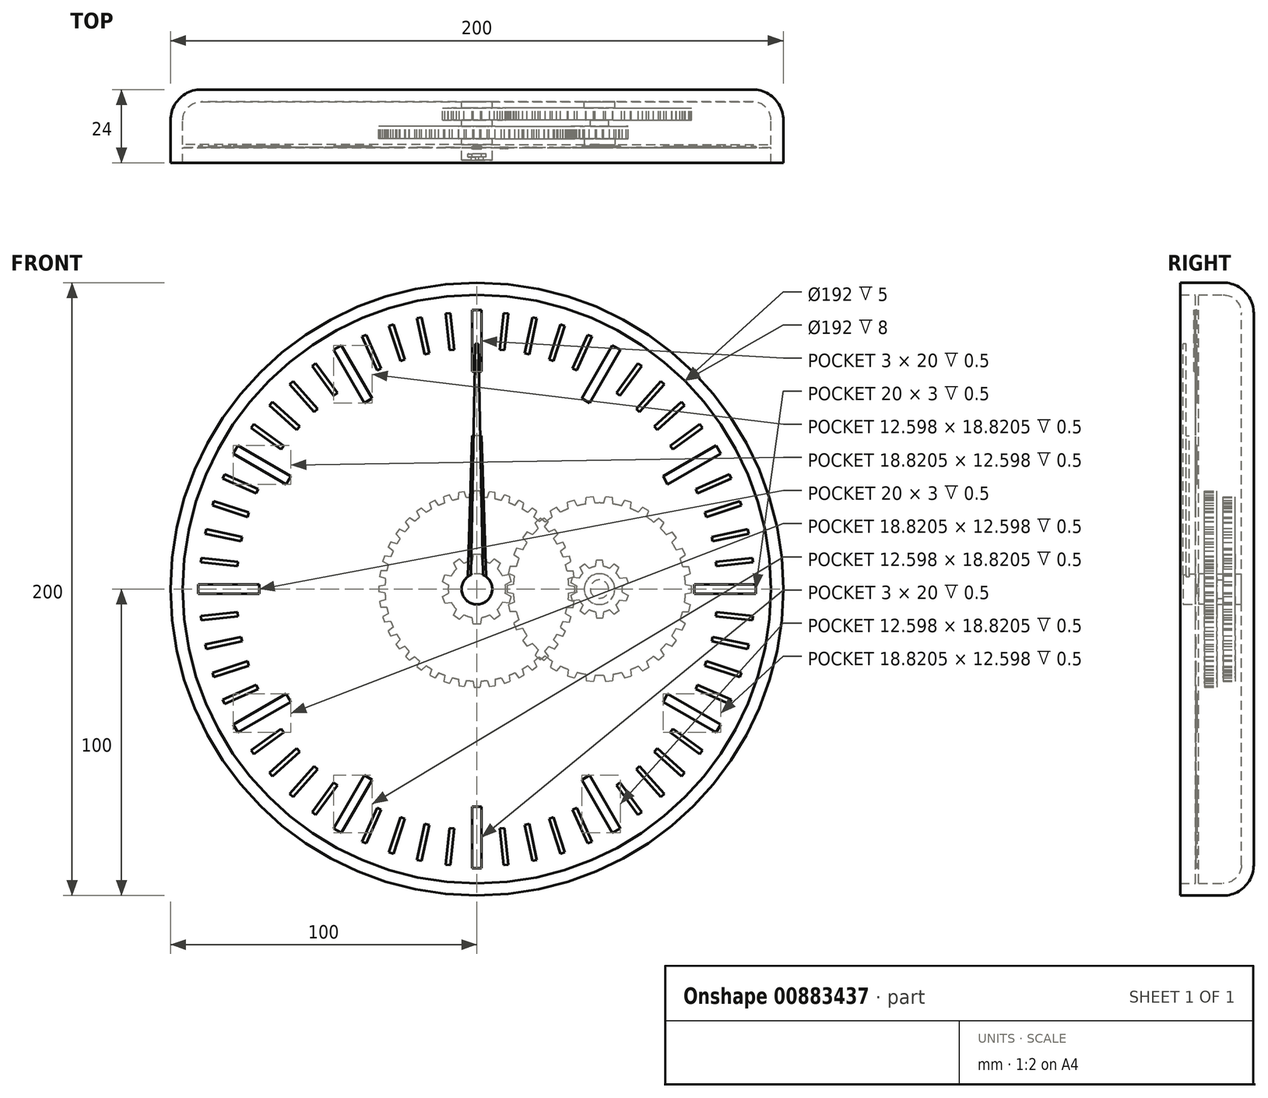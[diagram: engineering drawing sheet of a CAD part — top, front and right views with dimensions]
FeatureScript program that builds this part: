
annotation { "Feature Type Name" : "Feature", "Feature Type Description" : "" }
export const myFeature = defineFeature(function(context is Context, id is Id, definition is map)
    precondition{}
    {
        {
            var Q0;
            Q0=qCreatedBy(makeId("Front.planeOp"),FACE);
            var sketch = newSketch(context, id + "F0", { "sketchPlane" : qUnion([Q0])});
            skCircle(sketch, "E0", {"center": v(0, 0) * mm, "radius": 100 * mm});
            skSolve(sketch);
        }
        {
            var Q0;
            Q0 = qSketchRegion(id + "F0", true);
            extrude(context, id + "F1", {"entities" : qUnion([Q0]), "depth" : 24 * mm, "offsetDistance" : 25 * mm});
        }
        {
            var Q0;
            Q0=makeQuery(id+"F1.opExtrude","CAP_EDGE",EDGE,{"disambiguationData":[OSD([sQuery(id+"F0.wireOp",EDGE,"E0")])],"isStart":true});
            fillet(context, id + "F2", {"entities" : qUnion([Q0]), "radius" : 10 * mm, "tangentPropagation" : true, "allowEdgeOverflow" : false});
        }
        {
            var Q0;
            Q0=makeQuery(id+"F1.opExtrude","CAP_FACE",FACE,{"disambiguationData":[OSD([sQuery(id+"F0.wireOp",EDGE,"E0")])],"isStart":false});
            shell(context, id + "F3", {"entities" : qUnion([Q0]), "thickness" : 4 * mm});
        }
        {
            var Q0;
            {var subQ0=sQuery(id+"F0.wireOp",EDGE,"E0");Q0=makeQuery(id+"F3.opShell","OFFSET_FACE",FACE,{"disambiguationData":[OSD([subQ0]),TDD([makeQuery(id+"F1.opExtrude","CAP_FACE",FACE,{"disambiguationData":[OSD([subQ0])],"isStart":true})])]});}
            var sketch = newSketch(context, id + "F4", { "sketchPlane" : qUnion([Q0])});
            skCircle(sketch, "E1", {"center": v(0, 0) * mm, "radius": 3 * mm});
            skCircle(sketch, "E2", {"center": v(0, 0) * mm, "radius": 5 * mm});
            skCircle(sketch, "E3", {"center": v(40, 0) * mm, "radius": 3 * mm});
            skCircle(sketch, "E4", {"center": v(40, 0) * mm, "radius": 5 * mm});
            skSolve(sketch);
        }
        {
            var Q0;
            Q0 = qSketchRegion(id + "F4", true);
            extrude(context, id + "F5", {"entities" : qUnion([Q0]), "operationType" : NewBodyOperationType.ADD, "depth" : 2 * mm, "offsetDistance" : 25 * mm});
        }
        {
            var Q0;
            {var subQ0=sQuery(id+"F0.wireOp",EDGE,"E0");Q0=makeQuery(id+"F5.boolean.opBoolean","SPLIT",FACE,{"disambiguationData":[TD([makeQuery(id+"F5.opExtrude","SWEPT_FACE",FACE,{"disambiguationData":[OSD([sQuery(id+"F4.wireOp",EDGE,"E1")])]})])],"derivedFrom":makeQuery(id+"F3.opShell","OFFSET_FACE",FACE,{"disambiguationData":[OSD([subQ0]),TDD([makeQuery(id+"F1.opExtrude","CAP_FACE",FACE,{"disambiguationData":[OSD([subQ0])],"isStart":true})])]})});}
            extrude(context, id + "F6", {"entities" : qUnion([Q0]), "depth" : 19 * mm, "offsetDistance" : 25 * mm});
        }
        {
            var Q0;
            {var subQ0=sQuery(id+"F0.wireOp",EDGE,"E0");Q0=makeQuery(id+"F5.boolean.opBoolean","SPLIT",FACE,{"disambiguationData":[TD([makeQuery(id+"F5.opExtrude","SWEPT_FACE",FACE,{"disambiguationData":[OSD([sQuery(id+"F4.wireOp",EDGE,"E3")])]})])],"derivedFrom":makeQuery(id+"F3.opShell","OFFSET_FACE",FACE,{"disambiguationData":[OSD([subQ0]),TDD([makeQuery(id+"F1.opExtrude","CAP_FACE",FACE,{"disambiguationData":[OSD([subQ0])],"isStart":true})])]})});}
            extrude(context, id + "F7", {"entities" : qUnion([Q0]), "depth" : 8 * mm, "offsetDistance" : 25 * mm});
        }
        {
            var Q0;
            Q0=makeQuery(id+"F5.opExtrude","CAP_FACE",FACE,{"disambiguationData":[OSD([sQuery(id+"F4.wireOp",EDGE,"E1"),sQuery(id+"F4.wireOp",EDGE,"E2")])],"isStart":false});
            var sketch = newSketch(context, id + "F8", { "sketchPlane" : qUnion([Q0])});
            skCircle(sketch, "E5", {"center": v(0, 0) * mm, "radius": 9.38 * mm});
            skLineSegment(sketch, "E6", {"start": v(0, 11.38) * mm, "end": v(1.18, 11.38) * mm});
            skLineSegment(sketch, "E7", {"start": v(1.18, 11.38) * mm, "end": v(1.55, 9.25) * mm});
            skLineSegment(sketch, "E8.MirrorCS", {"start": v(0, 11.38) * mm, "end": v(-1.18, 11.38) * mm});
            skLineSegment(sketch, "E9.MirrorCS", {"start": v(-1.18, 11.38) * mm, "end": v(-1.55, 9.25) * mm});
            skLineSegment(sketch, "E10.1.0", {"start": v(-6.69, 9.2) * mm, "end": v(-5.73, 9.9) * mm});
            skLineSegment(sketch, "E10.1.1", {"start": v(-5.73, 9.9) * mm, "end": v(-4.18, 8.4) * mm});
            skLineSegment(sketch, "E10.1.2", {"start": v(-6.69, 9.2) * mm, "end": v(-7.64, 8.51) * mm});
            skLineSegment(sketch, "E10.1.3", {"start": v(-7.64, 8.51) * mm, "end": v(-6.7, 6.57) * mm});
            skLineSegment(sketch, "E10.2.0", {"start": v(-10.82, 3.52) * mm, "end": v(-10.45, 4.64) * mm});
            skLineSegment(sketch, "E10.2.1", {"start": v(-10.45, 4.64) * mm, "end": v(-8.31, 4.33) * mm});
            skLineSegment(sketch, "E10.2.2", {"start": v(-10.82, 3.52) * mm, "end": v(-11.18, 2.4) * mm});
            skLineSegment(sketch, "E10.2.3", {"start": v(-11.18, 2.4) * mm, "end": v(-9.27, 1.38) * mm});
            skLineSegment(sketch, "E11.1.3.0", {"start": v(-10.82, -3.52) * mm, "end": v(-11.18, -2.4) * mm});
            skLineSegment(sketch, "E11.3.3.0", {"start": v(-11.18, -2.4) * mm, "end": v(-9.27, -1.38) * mm});
            skLineSegment(sketch, "E11.6.3.0", {"start": v(-10.82, -3.52) * mm, "end": v(-10.45, -4.64) * mm});
            skLineSegment(sketch, "E11.9.3.0", {"start": v(-10.45, -4.64) * mm, "end": v(-8.31, -4.33) * mm});
            skLineSegment(sketch, "E11.1.4.0", {"start": v(-6.69, -9.2) * mm, "end": v(-7.64, -8.51) * mm});
            skLineSegment(sketch, "E11.3.4.0", {"start": v(-7.64, -8.51) * mm, "end": v(-6.7, -6.57) * mm});
            skLineSegment(sketch, "E11.6.4.0", {"start": v(-6.69, -9.2) * mm, "end": v(-5.73, -9.9) * mm});
            skLineSegment(sketch, "E11.9.4.0", {"start": v(-5.73, -9.9) * mm, "end": v(-4.18, -8.4) * mm});
            skLineSegment(sketch, "E11.1.5.0", {"start": v(0, -11.38) * mm, "end": v(-1.18, -11.38) * mm});
            skLineSegment(sketch, "E11.3.5.0", {"start": v(-1.18, -11.38) * mm, "end": v(-1.55, -9.25) * mm});
            skLineSegment(sketch, "E11.6.5.0", {"start": v(0, -11.38) * mm, "end": v(1.18, -11.38) * mm});
            skLineSegment(sketch, "E11.9.5.0", {"start": v(1.18, -11.38) * mm, "end": v(1.55, -9.25) * mm});
            skLineSegment(sketch, "E11.1.6.0", {"start": v(6.69, -9.2) * mm, "end": v(5.73, -9.9) * mm});
            skLineSegment(sketch, "E11.3.6.0", {"start": v(5.73, -9.9) * mm, "end": v(4.18, -8.4) * mm});
            skLineSegment(sketch, "E11.6.6.0", {"start": v(6.69, -9.2) * mm, "end": v(7.64, -8.51) * mm});
            skLineSegment(sketch, "E11.9.6.0", {"start": v(7.64, -8.51) * mm, "end": v(6.7, -6.57) * mm});
            skLineSegment(sketch, "E11.1.7.0", {"start": v(10.82, -3.52) * mm, "end": v(10.45, -4.64) * mm});
            skLineSegment(sketch, "E11.3.7.0", {"start": v(10.45, -4.64) * mm, "end": v(8.31, -4.33) * mm});
            skLineSegment(sketch, "E11.6.7.0", {"start": v(10.82, -3.52) * mm, "end": v(11.18, -2.4) * mm});
            skLineSegment(sketch, "E11.9.7.0", {"start": v(11.18, -2.4) * mm, "end": v(9.27, -1.38) * mm});
            skLineSegment(sketch, "E11.1.8.0", {"start": v(10.82, 3.52) * mm, "end": v(11.18, 2.4) * mm});
            skLineSegment(sketch, "E11.3.8.0", {"start": v(11.18, 2.4) * mm, "end": v(9.27, 1.38) * mm});
            skLineSegment(sketch, "E11.6.8.0", {"start": v(10.82, 3.52) * mm, "end": v(10.45, 4.64) * mm});
            skLineSegment(sketch, "E11.9.8.0", {"start": v(10.45, 4.64) * mm, "end": v(8.31, 4.33) * mm});
            skLineSegment(sketch, "E11.1.9.0", {"start": v(6.69, 9.2) * mm, "end": v(7.64, 8.51) * mm});
            skLineSegment(sketch, "E11.3.9.0", {"start": v(7.64, 8.51) * mm, "end": v(6.7, 6.57) * mm});
            skLineSegment(sketch, "E11.6.9.0", {"start": v(6.69, 9.2) * mm, "end": v(5.73, 9.9) * mm});
            skLineSegment(sketch, "E11.9.9.0", {"start": v(5.73, 9.9) * mm, "end": v(4.18, 8.4) * mm});
            skSolve(sketch);
        }
        {
            var Q0;
            Q0 = qSketchRegion(id + "F8", true);
            extrude(context, id + "F9", {"entities" : qUnion([Q0]), "operationType" : NewBodyOperationType.ADD, "depth" : 4 * mm, "offsetDistance" : 25 * mm});
        }
        {
            var Q0;
            Q0=makeQuery(id+"F5.opExtrude","CAP_FACE",FACE,{"disambiguationData":[OSD([sQuery(id+"F4.wireOp",EDGE,"E3"),sQuery(id+"F4.wireOp",EDGE,"E4")])],"isStart":false});
            var sketch = newSketch(context, id + "F10", { "sketchPlane" : qUnion([Q0])});
            skCircle(sketch, "E12", {"center": v(40, 0) * mm, "radius": 28.12 * mm});
            skLineSegment(sketch, "E13", {"start": v(11.92, 1.54) * mm, "end": v(9.88, 1.18) * mm});
            skLineSegment(sketch, "E14", {"start": v(9.88, 1.18) * mm, "end": v(9.88, 0) * mm});
            skLineSegment(sketch, "E15.MirrorCS", {"start": v(9.88, -1.18) * mm, "end": v(9.88, 0) * mm});
            skLineSegment(sketch, "E16.MirrorCS", {"start": v(11.92, -1.54) * mm, "end": v(9.88, -1.18) * mm});
            skLineSegment(sketch, "E17.1.0", {"start": v(12.21, -4.33) * mm, "end": v(10.29, -5.11) * mm});
            skLineSegment(sketch, "E17.1.1", {"start": v(10.29, -5.11) * mm, "end": v(10.53, -6.26) * mm});
            skLineSegment(sketch, "E17.1.2", {"start": v(10.78, -7.42) * mm, "end": v(10.53, -6.26) * mm});
            skLineSegment(sketch, "E17.1.3", {"start": v(12.85, -7.34) * mm, "end": v(10.78, -7.42) * mm});
            skLineSegment(sketch, "E17.2.0", {"start": v(13.72, -10.02) * mm, "end": v(12, -11.18) * mm});
            skLineSegment(sketch, "E17.2.1", {"start": v(12, -11.18) * mm, "end": v(12.48, -12.25) * mm});
            skLineSegment(sketch, "E17.2.2", {"start": v(12.96, -13.33) * mm, "end": v(12.48, -12.25) * mm});
            skLineSegment(sketch, "E17.2.3", {"start": v(14.97, -12.83) * mm, "end": v(12.96, -13.33) * mm});
            skLineSegment(sketch, "E18.2.3.0", {"start": v(16.38, -15.26) * mm, "end": v(14.94, -16.75) * mm});
            skLineSegment(sketch, "E18.3.3.0", {"start": v(14.94, -16.75) * mm, "end": v(15.63, -17.7) * mm});
            skLineSegment(sketch, "E18.6.3.0", {"start": v(16.32, -18.66) * mm, "end": v(15.63, -17.7) * mm});
            skLineSegment(sketch, "E18.9.3.0", {"start": v(18.18, -17.75) * mm, "end": v(16.32, -18.66) * mm});
            skLineSegment(sketch, "E18.2.4.0", {"start": v(20.07, -19.84) * mm, "end": v(18.97, -21.6) * mm});
            skLineSegment(sketch, "E18.3.4.0", {"start": v(18.97, -21.6) * mm, "end": v(19.84, -22.39) * mm});
            skLineSegment(sketch, "E18.6.4.0", {"start": v(20.72, -23.18) * mm, "end": v(19.84, -22.39) * mm});
            skLineSegment(sketch, "E18.9.4.0", {"start": v(22.35, -21.9) * mm, "end": v(20.72, -23.18) * mm});
            skLineSegment(sketch, "E18.2.5.0", {"start": v(24.63, -23.55) * mm, "end": v(23.92, -25.5) * mm});
            skLineSegment(sketch, "E18.3.5.0", {"start": v(23.92, -25.5) * mm, "end": v(24.94, -26.09) * mm});
            skLineSegment(sketch, "E18.6.5.0", {"start": v(25.96, -26.68) * mm, "end": v(24.94, -26.09) * mm});
            skLineSegment(sketch, "E18.9.5.0", {"start": v(27.3, -25.09) * mm, "end": v(25.96, -26.68) * mm});
            skLineSegment(sketch, "E18.2.6.0", {"start": v(29.86, -26.23) * mm, "end": v(29.57, -28.29) * mm});
            skLineSegment(sketch, "E18.3.6.0", {"start": v(29.57, -28.29) * mm, "end": v(30.7, -28.65) * mm});
            skLineSegment(sketch, "E18.6.6.0", {"start": v(31.81, -29.01) * mm, "end": v(30.7, -28.65) * mm});
            skLineSegment(sketch, "E18.9.6.0", {"start": v(32.78, -27.18) * mm, "end": v(31.81, -29.01) * mm});
            skLineSegment(sketch, "E18.2.7.0", {"start": v(35.53, -27.77) * mm, "end": v(35.68, -29.84) * mm});
            skLineSegment(sketch, "E18.3.7.0", {"start": v(35.68, -29.84) * mm, "end": v(36.85, -29.96) * mm});
            skLineSegment(sketch, "E18.6.7.0", {"start": v(38.02, -30.08) * mm, "end": v(36.85, -29.96) * mm});
            skLineSegment(sketch, "E18.9.7.0", {"start": v(38.6, -28.09) * mm, "end": v(38.02, -30.08) * mm});
            skLineSegment(sketch, "E18.2.8.0", {"start": v(41.4, -28.09) * mm, "end": v(41.98, -30.08) * mm});
            skLineSegment(sketch, "E18.3.8.0", {"start": v(41.98, -30.08) * mm, "end": v(43.15, -29.96) * mm});
            skLineSegment(sketch, "E18.6.8.0", {"start": v(44.32, -29.84) * mm, "end": v(43.15, -29.96) * mm});
            skLineSegment(sketch, "E18.9.8.0", {"start": v(44.47, -27.77) * mm, "end": v(44.32, -29.84) * mm});
            skLineSegment(sketch, "E18.2.9.0", {"start": v(47.22, -27.18) * mm, "end": v(48.19, -29.01) * mm});
            skLineSegment(sketch, "E18.3.9.0", {"start": v(48.19, -29.01) * mm, "end": v(49.3, -28.65) * mm});
            skLineSegment(sketch, "E18.6.9.0", {"start": v(50.43, -28.29) * mm, "end": v(49.3, -28.65) * mm});
            skLineSegment(sketch, "E18.9.9.0", {"start": v(50.14, -26.23) * mm, "end": v(50.43, -28.29) * mm});
            skLineSegment(sketch, "E18.2.10.0", {"start": v(52.7, -25.09) * mm, "end": v(54.04, -26.68) * mm});
            skLineSegment(sketch, "E18.3.10.0", {"start": v(54.04, -26.68) * mm, "end": v(55.06, -26.09) * mm});
            skLineSegment(sketch, "E18.6.10.0", {"start": v(56.08, -25.5) * mm, "end": v(55.06, -26.09) * mm});
            skLineSegment(sketch, "E18.9.10.0", {"start": v(55.37, -23.55) * mm, "end": v(56.08, -25.5) * mm});
            skLineSegment(sketch, "E18.2.11.0", {"start": v(57.65, -21.9) * mm, "end": v(59.28, -23.18) * mm});
            skLineSegment(sketch, "E18.3.11.0", {"start": v(59.28, -23.18) * mm, "end": v(60.16, -22.39) * mm});
            skLineSegment(sketch, "E18.6.11.0", {"start": v(61.03, -21.6) * mm, "end": v(60.16, -22.39) * mm});
            skLineSegment(sketch, "E18.9.11.0", {"start": v(59.93, -19.84) * mm, "end": v(61.03, -21.6) * mm});
            skLineSegment(sketch, "E18.2.12.0", {"start": v(61.82, -17.75) * mm, "end": v(63.68, -18.66) * mm});
            skLineSegment(sketch, "E18.3.12.0", {"start": v(63.68, -18.66) * mm, "end": v(64.37, -17.7) * mm});
            skLineSegment(sketch, "E18.6.12.0", {"start": v(65.06, -16.75) * mm, "end": v(64.37, -17.7) * mm});
            skLineSegment(sketch, "E18.9.12.0", {"start": v(63.62, -15.26) * mm, "end": v(65.06, -16.75) * mm});
            skLineSegment(sketch, "E18.2.13.0", {"start": v(65.03, -12.83) * mm, "end": v(67.04, -13.33) * mm});
            skLineSegment(sketch, "E18.3.13.0", {"start": v(67.04, -13.33) * mm, "end": v(67.52, -12.25) * mm});
            skLineSegment(sketch, "E18.6.13.0", {"start": v(68, -11.18) * mm, "end": v(67.52, -12.25) * mm});
            skLineSegment(sketch, "E18.9.13.0", {"start": v(66.28, -10.02) * mm, "end": v(68, -11.18) * mm});
            skLineSegment(sketch, "E18.2.14.0", {"start": v(67.15, -7.34) * mm, "end": v(69.22, -7.42) * mm});
            skLineSegment(sketch, "E18.3.14.0", {"start": v(69.22, -7.42) * mm, "end": v(69.47, -6.26) * mm});
            skLineSegment(sketch, "E18.6.14.0", {"start": v(69.71, -5.11) * mm, "end": v(69.47, -6.26) * mm});
            skLineSegment(sketch, "E18.9.14.0", {"start": v(67.79, -4.33) * mm, "end": v(69.71, -5.11) * mm});
            skLineSegment(sketch, "E18.2.15.0", {"start": v(68.08, -1.54) * mm, "end": v(70.12, -1.18) * mm});
            skLineSegment(sketch, "E18.3.15.0", {"start": v(70.12, -1.18) * mm, "end": v(70.12, 0) * mm});
            skLineSegment(sketch, "E18.6.15.0", {"start": v(70.12, 1.18) * mm, "end": v(70.12, 0) * mm});
            skLineSegment(sketch, "E18.9.15.0", {"start": v(68.08, 1.54) * mm, "end": v(70.12, 1.18) * mm});
            skLineSegment(sketch, "E18.2.16.0", {"start": v(67.79, 4.33) * mm, "end": v(69.71, 5.11) * mm});
            skLineSegment(sketch, "E18.3.16.0", {"start": v(69.71, 5.11) * mm, "end": v(69.47, 6.26) * mm});
            skLineSegment(sketch, "E18.6.16.0", {"start": v(69.22, 7.42) * mm, "end": v(69.47, 6.26) * mm});
            skLineSegment(sketch, "E18.9.16.0", {"start": v(67.15, 7.34) * mm, "end": v(69.22, 7.42) * mm});
            skLineSegment(sketch, "E18.2.17.0", {"start": v(66.28, 10.02) * mm, "end": v(68, 11.18) * mm});
            skLineSegment(sketch, "E18.3.17.0", {"start": v(68, 11.18) * mm, "end": v(67.52, 12.25) * mm});
            skLineSegment(sketch, "E18.6.17.0", {"start": v(67.04, 13.33) * mm, "end": v(67.52, 12.25) * mm});
            skLineSegment(sketch, "E18.9.17.0", {"start": v(65.03, 12.83) * mm, "end": v(67.04, 13.33) * mm});
            skLineSegment(sketch, "E18.2.18.0", {"start": v(63.62, 15.26) * mm, "end": v(65.06, 16.75) * mm});
            skLineSegment(sketch, "E18.3.18.0", {"start": v(65.06, 16.75) * mm, "end": v(64.37, 17.7) * mm});
            skLineSegment(sketch, "E18.6.18.0", {"start": v(63.68, 18.66) * mm, "end": v(64.37, 17.7) * mm});
            skLineSegment(sketch, "E18.9.18.0", {"start": v(61.82, 17.75) * mm, "end": v(63.68, 18.66) * mm});
            skLineSegment(sketch, "E18.2.19.0", {"start": v(59.93, 19.84) * mm, "end": v(61.03, 21.6) * mm});
            skLineSegment(sketch, "E18.3.19.0", {"start": v(61.03, 21.6) * mm, "end": v(60.16, 22.39) * mm});
            skLineSegment(sketch, "E18.6.19.0", {"start": v(59.28, 23.18) * mm, "end": v(60.16, 22.39) * mm});
            skLineSegment(sketch, "E18.9.19.0", {"start": v(57.65, 21.9) * mm, "end": v(59.28, 23.18) * mm});
            skLineSegment(sketch, "E18.2.20.0", {"start": v(55.37, 23.55) * mm, "end": v(56.08, 25.5) * mm});
            skLineSegment(sketch, "E18.3.20.0", {"start": v(56.08, 25.5) * mm, "end": v(55.06, 26.09) * mm});
            skLineSegment(sketch, "E18.6.20.0", {"start": v(54.04, 26.68) * mm, "end": v(55.06, 26.09) * mm});
            skLineSegment(sketch, "E18.9.20.0", {"start": v(52.7, 25.09) * mm, "end": v(54.04, 26.68) * mm});
            skLineSegment(sketch, "E18.2.21.0", {"start": v(50.14, 26.23) * mm, "end": v(50.43, 28.29) * mm});
            skLineSegment(sketch, "E18.3.21.0", {"start": v(50.43, 28.29) * mm, "end": v(49.3, 28.65) * mm});
            skLineSegment(sketch, "E18.6.21.0", {"start": v(48.19, 29.01) * mm, "end": v(49.3, 28.65) * mm});
            skLineSegment(sketch, "E18.9.21.0", {"start": v(47.22, 27.18) * mm, "end": v(48.19, 29.01) * mm});
            skLineSegment(sketch, "E18.2.22.0", {"start": v(44.47, 27.77) * mm, "end": v(44.32, 29.84) * mm});
            skLineSegment(sketch, "E18.3.22.0", {"start": v(44.32, 29.84) * mm, "end": v(43.15, 29.96) * mm});
            skLineSegment(sketch, "E18.6.22.0", {"start": v(41.98, 30.08) * mm, "end": v(43.15, 29.96) * mm});
            skLineSegment(sketch, "E18.9.22.0", {"start": v(41.4, 28.09) * mm, "end": v(41.98, 30.08) * mm});
            skLineSegment(sketch, "E18.2.23.0", {"start": v(38.6, 28.09) * mm, "end": v(38.02, 30.08) * mm});
            skLineSegment(sketch, "E18.3.23.0", {"start": v(38.02, 30.08) * mm, "end": v(36.85, 29.96) * mm});
            skLineSegment(sketch, "E18.6.23.0", {"start": v(35.68, 29.84) * mm, "end": v(36.85, 29.96) * mm});
            skLineSegment(sketch, "E18.9.23.0", {"start": v(35.53, 27.77) * mm, "end": v(35.68, 29.84) * mm});
            skLineSegment(sketch, "E18.2.24.0", {"start": v(32.78, 27.18) * mm, "end": v(31.81, 29.01) * mm});
            skLineSegment(sketch, "E18.3.24.0", {"start": v(31.81, 29.01) * mm, "end": v(30.7, 28.65) * mm});
            skLineSegment(sketch, "E18.6.24.0", {"start": v(29.57, 28.29) * mm, "end": v(30.7, 28.65) * mm});
            skLineSegment(sketch, "E18.9.24.0", {"start": v(29.86, 26.23) * mm, "end": v(29.57, 28.29) * mm});
            skLineSegment(sketch, "E18.2.25.0", {"start": v(27.3, 25.09) * mm, "end": v(25.96, 26.68) * mm});
            skLineSegment(sketch, "E18.3.25.0", {"start": v(25.96, 26.68) * mm, "end": v(24.94, 26.09) * mm});
            skLineSegment(sketch, "E18.6.25.0", {"start": v(23.92, 25.5) * mm, "end": v(24.94, 26.09) * mm});
            skLineSegment(sketch, "E18.9.25.0", {"start": v(24.63, 23.55) * mm, "end": v(23.92, 25.5) * mm});
            skLineSegment(sketch, "E18.2.26.0", {"start": v(22.35, 21.9) * mm, "end": v(20.72, 23.18) * mm});
            skLineSegment(sketch, "E18.3.26.0", {"start": v(20.72, 23.18) * mm, "end": v(19.84, 22.39) * mm});
            skLineSegment(sketch, "E18.6.26.0", {"start": v(18.97, 21.6) * mm, "end": v(19.84, 22.39) * mm});
            skLineSegment(sketch, "E18.9.26.0", {"start": v(20.07, 19.84) * mm, "end": v(18.97, 21.6) * mm});
            skLineSegment(sketch, "E18.2.27.0", {"start": v(18.18, 17.75) * mm, "end": v(16.32, 18.66) * mm});
            skLineSegment(sketch, "E18.3.27.0", {"start": v(16.32, 18.66) * mm, "end": v(15.63, 17.7) * mm});
            skLineSegment(sketch, "E18.6.27.0", {"start": v(14.94, 16.75) * mm, "end": v(15.63, 17.7) * mm});
            skLineSegment(sketch, "E18.9.27.0", {"start": v(16.38, 15.26) * mm, "end": v(14.94, 16.75) * mm});
            skLineSegment(sketch, "E18.2.28.0", {"start": v(14.97, 12.83) * mm, "end": v(12.96, 13.33) * mm});
            skLineSegment(sketch, "E18.3.28.0", {"start": v(12.96, 13.33) * mm, "end": v(12.48, 12.25) * mm});
            skLineSegment(sketch, "E18.6.28.0", {"start": v(12, 11.18) * mm, "end": v(12.48, 12.25) * mm});
            skLineSegment(sketch, "E18.9.28.0", {"start": v(13.72, 10.02) * mm, "end": v(12, 11.18) * mm});
            skLineSegment(sketch, "E18.2.29.0", {"start": v(12.85, 7.34) * mm, "end": v(10.78, 7.42) * mm});
            skLineSegment(sketch, "E18.3.29.0", {"start": v(10.78, 7.42) * mm, "end": v(10.53, 6.26) * mm});
            skLineSegment(sketch, "E18.6.29.0", {"start": v(10.29, 5.11) * mm, "end": v(10.53, 6.26) * mm});
            skLineSegment(sketch, "E18.9.29.0", {"start": v(12.21, 4.33) * mm, "end": v(10.29, 5.11) * mm});
            skSolve(sketch);
        }
        {
            var Q0;
            Q0 = qSketchRegion(id + "F10", true);
            extrude(context, id + "F11", {"entities" : qUnion([Q0]), "operationType" : NewBodyOperationType.ADD, "depth" : 4 * mm, "offsetDistance" : 25 * mm});
        }
        {
            var Q0;
            Q0=makeQuery(id+"F9.opExtrude","CAP_FACE",FACE,{"disambiguationData":[OSD([sQuery(id+"F8.wireOp",EDGE,"E5"),sQuery(id+"F8.wireOp",EDGE,"E6"),sQuery(id+"F8.wireOp",EDGE,"E7"),sQuery(id+"F8.wireOp",EDGE,"E8.MirrorCS"),sQuery(id+"F8.wireOp",EDGE,"E9.MirrorCS"),sQuery(id+"F8.wireOp",EDGE,"E10.1.0"),sQuery(id+"F8.wireOp",EDGE,"E10.1.1"),sQuery(id+"F8.wireOp",EDGE,"E10.1.2"),sQuery(id+"F8.wireOp",EDGE,"E10.1.3"),sQuery(id+"F8.wireOp",EDGE,"E10.2.0"),sQuery(id+"F8.wireOp",EDGE,"E10.2.1"),sQuery(id+"F8.wireOp",EDGE,"E10.2.2"),sQuery(id+"F8.wireOp",EDGE,"E10.2.3"),sQuery(id+"F8.wireOp",EDGE,"E11.1.3.0"),sQuery(id+"F8.wireOp",EDGE,"E11.3.3.0"),sQuery(id+"F8.wireOp",EDGE,"E11.6.3.0"),sQuery(id+"F8.wireOp",EDGE,"E11.9.3.0"),sQuery(id+"F8.wireOp",EDGE,"E11.1.4.0"),sQuery(id+"F8.wireOp",EDGE,"E11.3.4.0"),sQuery(id+"F8.wireOp",EDGE,"E11.6.4.0"),sQuery(id+"F8.wireOp",EDGE,"E11.9.4.0"),sQuery(id+"F8.wireOp",EDGE,"E11.1.5.0"),sQuery(id+"F8.wireOp",EDGE,"E11.3.5.0"),sQuery(id+"F8.wireOp",EDGE,"E11.6.5.0"),sQuery(id+"F8.wireOp",EDGE,"E11.9.5.0"),sQuery(id+"F8.wireOp",EDGE,"E11.1.6.0"),sQuery(id+"F8.wireOp",EDGE,"E11.3.6.0"),sQuery(id+"F8.wireOp",EDGE,"E11.6.6.0"),sQuery(id+"F8.wireOp",EDGE,"E11.9.6.0"),sQuery(id+"F8.wireOp",EDGE,"E11.1.7.0"),sQuery(id+"F8.wireOp",EDGE,"E11.3.7.0"),sQuery(id+"F8.wireOp",EDGE,"E11.6.7.0"),sQuery(id+"F8.wireOp",EDGE,"E11.9.7.0"),sQuery(id+"F8.wireOp",EDGE,"E11.1.8.0"),sQuery(id+"F8.wireOp",EDGE,"E11.3.8.0"),sQuery(id+"F8.wireOp",EDGE,"E11.6.8.0"),sQuery(id+"F8.wireOp",EDGE,"E11.9.8.0"),sQuery(id+"F8.wireOp",EDGE,"E11.1.9.0"),sQuery(id+"F8.wireOp",EDGE,"E11.3.9.0"),sQuery(id+"F8.wireOp",EDGE,"E11.6.9.0"),sQuery(id+"F8.wireOp",EDGE,"E11.9.9.0")])],"isStart":false});
            var sketch = newSketch(context, id + "F12", { "sketchPlane" : qUnion([Q0])});
            skCircle(sketch, "E19.0", {"center": v(0, 0) * mm, "radius": 5 * mm});
            skCircle(sketch, "E20.0", {"center": v(0, 0) * mm, "radius": 3 * mm});
            skSolve(sketch);
        }
        {
            var Q0;
            Q0 = qSketchRegion(id + "F12", true);
            extrude(context, id + "F13", {"entities" : qUnion([Q0]), "depth" : 2 * mm, "offsetDistance" : 25 * mm});
        }
        {
            var Q0;
            Q0=makeQuery(id+"F13.opExtrude","CAP_FACE",FACE,{"disambiguationData":[OSD([sQuery(id+"F12.wireOp",EDGE,"E19.0"),sQuery(id+"F12.wireOp",EDGE,"E20.0")])],"isStart":false});
            var sketch = newSketch(context, id + "F14", { "sketchPlane" : qUnion([Q0])});
            skCircle(sketch, "E21.0", {"center": v(0, 0) * mm, "radius": 3 * mm});
            skCircle(sketch, "E22", {"center": v(0, 0) * mm, "radius": 30 * mm});
            skLineSegment(sketch, "E23", {"start": v(1.3, 29.97) * mm, "end": v(0.94, 32) * mm});
            skLineSegment(sketch, "E24", {"start": v(0.94, 32) * mm, "end": v(0, 32) * mm});
            skLineSegment(sketch, "E25.MirrorCS", {"start": v(-1.3, 29.97) * mm, "end": v(-0.94, 32) * mm});
            skLineSegment(sketch, "E26.MirrorCS", {"start": v(-0.94, 32) * mm, "end": v(0, 32) * mm});
            skLineSegment(sketch, "E27.1.0", {"start": v(-5.94, 31.46) * mm, "end": v(-5, 31.6) * mm});
            skLineSegment(sketch, "E27.1.1", {"start": v(-4.08, 31.75) * mm, "end": v(-5, 31.6) * mm});
            skLineSegment(sketch, "E27.1.2", {"start": v(-3.4, 29.8) * mm, "end": v(-4.08, 31.75) * mm});
            skLineSegment(sketch, "E27.1.3", {"start": v(-5.97, 29.4) * mm, "end": v(-5.94, 31.46) * mm});
            skLineSegment(sketch, "E27.2.0", {"start": v(-10.78, 30.14) * mm, "end": v(-9.89, 30.43) * mm});
            skLineSegment(sketch, "E27.2.1", {"start": v(-9, 30.73) * mm, "end": v(-9.89, 30.43) * mm});
            skLineSegment(sketch, "E27.2.2", {"start": v(-8.03, 28.9) * mm, "end": v(-9, 30.73) * mm});
            skLineSegment(sketch, "E27.2.3", {"start": v(-10.5, 28.1) * mm, "end": v(-10.78, 30.14) * mm});
            skLineSegment(sketch, "E28.1.3.0", {"start": v(-15.37, 28.08) * mm, "end": v(-14.53, 28.51) * mm});
            skLineSegment(sketch, "E28.3.3.0", {"start": v(-13.69, 28.94) * mm, "end": v(-14.53, 28.51) * mm});
            skLineSegment(sketch, "E28.6.3.0", {"start": v(-12.45, 27.3) * mm, "end": v(-13.69, 28.94) * mm});
            skLineSegment(sketch, "E28.9.3.0", {"start": v(-14.77, 26.11) * mm, "end": v(-15.37, 28.08) * mm});
            skLineSegment(sketch, "E28.1.4.0", {"start": v(-19.57, 25.33) * mm, "end": v(-18.8, 25.89) * mm});
            skLineSegment(sketch, "E28.3.4.0", {"start": v(-18.05, 26.44) * mm, "end": v(-18.8, 25.89) * mm});
            skLineSegment(sketch, "E28.6.4.0", {"start": v(-16.57, 25.01) * mm, "end": v(-18.05, 26.44) * mm});
            skLineSegment(sketch, "E28.9.4.0", {"start": v(-18.67, 23.48) * mm, "end": v(-19.57, 25.33) * mm});
            skLineSegment(sketch, "E28.1.5.0", {"start": v(-23.3, 21.96) * mm, "end": v(-22.63, 22.63) * mm});
            skLineSegment(sketch, "E28.3.5.0", {"start": v(-21.96, 23.3) * mm, "end": v(-22.63, 22.63) * mm});
            skLineSegment(sketch, "E28.6.5.0", {"start": v(-20.27, 22.11) * mm, "end": v(-21.96, 23.3) * mm});
            skLineSegment(sketch, "E28.9.5.0", {"start": v(-22.11, 20.27) * mm, "end": v(-23.3, 21.96) * mm});
            skLineSegment(sketch, "E28.1.6.0", {"start": v(-26.44, 18.05) * mm, "end": v(-25.89, 18.8) * mm});
            skLineSegment(sketch, "E28.3.6.0", {"start": v(-25.33, 19.57) * mm, "end": v(-25.89, 18.8) * mm});
            skLineSegment(sketch, "E28.6.6.0", {"start": v(-23.48, 18.67) * mm, "end": v(-25.33, 19.57) * mm});
            skLineSegment(sketch, "E28.9.6.0", {"start": v(-25.01, 16.57) * mm, "end": v(-26.44, 18.05) * mm});
            skLineSegment(sketch, "E28.1.7.0", {"start": v(-28.94, 13.69) * mm, "end": v(-28.51, 14.53) * mm});
            skLineSegment(sketch, "E28.3.7.0", {"start": v(-28.08, 15.37) * mm, "end": v(-28.51, 14.53) * mm});
            skLineSegment(sketch, "E28.6.7.0", {"start": v(-26.11, 14.77) * mm, "end": v(-28.08, 15.37) * mm});
            skLineSegment(sketch, "E28.9.7.0", {"start": v(-27.3, 12.45) * mm, "end": v(-28.94, 13.69) * mm});
            skLineSegment(sketch, "E28.1.8.0", {"start": v(-30.73, 9) * mm, "end": v(-30.43, 9.89) * mm});
            skLineSegment(sketch, "E28.3.8.0", {"start": v(-30.14, 10.78) * mm, "end": v(-30.43, 9.89) * mm});
            skLineSegment(sketch, "E28.6.8.0", {"start": v(-28.1, 10.5) * mm, "end": v(-30.14, 10.78) * mm});
            skLineSegment(sketch, "E28.9.8.0", {"start": v(-28.9, 8.03) * mm, "end": v(-30.73, 9) * mm});
            skLineSegment(sketch, "E28.1.9.0", {"start": v(-31.75, 4.08) * mm, "end": v(-31.6, 5) * mm});
            skLineSegment(sketch, "E28.3.9.0", {"start": v(-31.46, 5.94) * mm, "end": v(-31.6, 5) * mm});
            skLineSegment(sketch, "E28.6.9.0", {"start": v(-29.4, 5.97) * mm, "end": v(-31.46, 5.94) * mm});
            skLineSegment(sketch, "E28.9.9.0", {"start": v(-29.8, 3.4) * mm, "end": v(-31.75, 4.08) * mm});
            skLineSegment(sketch, "E28.1.10.0", {"start": v(-32, -0.94) * mm, "end": v(-32, 0) * mm});
            skLineSegment(sketch, "E28.3.10.0", {"start": v(-32, 0.94) * mm, "end": v(-32, 0) * mm});
            skLineSegment(sketch, "E28.6.10.0", {"start": v(-29.97, 1.3) * mm, "end": v(-32, 0.94) * mm});
            skLineSegment(sketch, "E28.9.10.0", {"start": v(-29.97, -1.3) * mm, "end": v(-32, -0.94) * mm});
            skLineSegment(sketch, "E28.1.11.0", {"start": v(-31.46, -5.94) * mm, "end": v(-31.6, -5) * mm});
            skLineSegment(sketch, "E28.3.11.0", {"start": v(-31.75, -4.08) * mm, "end": v(-31.6, -5) * mm});
            skLineSegment(sketch, "E28.6.11.0", {"start": v(-29.8, -3.4) * mm, "end": v(-31.75, -4.08) * mm});
            skLineSegment(sketch, "E28.9.11.0", {"start": v(-29.4, -5.97) * mm, "end": v(-31.46, -5.94) * mm});
            skLineSegment(sketch, "E28.1.12.0", {"start": v(-30.14, -10.78) * mm, "end": v(-30.43, -9.89) * mm});
            skLineSegment(sketch, "E28.3.12.0", {"start": v(-30.73, -9) * mm, "end": v(-30.43, -9.89) * mm});
            skLineSegment(sketch, "E28.6.12.0", {"start": v(-28.9, -8.03) * mm, "end": v(-30.73, -9) * mm});
            skLineSegment(sketch, "E28.9.12.0", {"start": v(-28.1, -10.5) * mm, "end": v(-30.14, -10.78) * mm});
            skLineSegment(sketch, "E28.1.13.0", {"start": v(-28.08, -15.37) * mm, "end": v(-28.51, -14.53) * mm});
            skLineSegment(sketch, "E28.3.13.0", {"start": v(-28.94, -13.69) * mm, "end": v(-28.51, -14.53) * mm});
            skLineSegment(sketch, "E28.6.13.0", {"start": v(-27.3, -12.45) * mm, "end": v(-28.94, -13.69) * mm});
            skLineSegment(sketch, "E28.9.13.0", {"start": v(-26.11, -14.77) * mm, "end": v(-28.08, -15.37) * mm});
            skLineSegment(sketch, "E28.1.14.0", {"start": v(-25.33, -19.57) * mm, "end": v(-25.89, -18.8) * mm});
            skLineSegment(sketch, "E28.3.14.0", {"start": v(-26.44, -18.05) * mm, "end": v(-25.89, -18.8) * mm});
            skLineSegment(sketch, "E28.6.14.0", {"start": v(-25.01, -16.57) * mm, "end": v(-26.44, -18.05) * mm});
            skLineSegment(sketch, "E28.9.14.0", {"start": v(-23.48, -18.67) * mm, "end": v(-25.33, -19.57) * mm});
            skLineSegment(sketch, "E28.1.15.0", {"start": v(-21.96, -23.3) * mm, "end": v(-22.63, -22.63) * mm});
            skLineSegment(sketch, "E28.3.15.0", {"start": v(-23.3, -21.96) * mm, "end": v(-22.63, -22.63) * mm});
            skLineSegment(sketch, "E28.6.15.0", {"start": v(-22.11, -20.27) * mm, "end": v(-23.3, -21.96) * mm});
            skLineSegment(sketch, "E28.9.15.0", {"start": v(-20.27, -22.11) * mm, "end": v(-21.96, -23.3) * mm});
            skLineSegment(sketch, "E28.1.16.0", {"start": v(-18.05, -26.44) * mm, "end": v(-18.8, -25.89) * mm});
            skLineSegment(sketch, "E28.3.16.0", {"start": v(-19.57, -25.33) * mm, "end": v(-18.8, -25.89) * mm});
            skLineSegment(sketch, "E28.6.16.0", {"start": v(-18.67, -23.48) * mm, "end": v(-19.57, -25.33) * mm});
            skLineSegment(sketch, "E28.9.16.0", {"start": v(-16.57, -25.01) * mm, "end": v(-18.05, -26.44) * mm});
            skLineSegment(sketch, "E28.1.17.0", {"start": v(-13.69, -28.94) * mm, "end": v(-14.53, -28.51) * mm});
            skLineSegment(sketch, "E28.3.17.0", {"start": v(-15.37, -28.08) * mm, "end": v(-14.53, -28.51) * mm});
            skLineSegment(sketch, "E28.6.17.0", {"start": v(-14.77, -26.11) * mm, "end": v(-15.37, -28.08) * mm});
            skLineSegment(sketch, "E28.9.17.0", {"start": v(-12.45, -27.3) * mm, "end": v(-13.69, -28.94) * mm});
            skLineSegment(sketch, "E28.1.18.0", {"start": v(-9, -30.73) * mm, "end": v(-9.89, -30.43) * mm});
            skLineSegment(sketch, "E28.3.18.0", {"start": v(-10.78, -30.14) * mm, "end": v(-9.89, -30.43) * mm});
            skLineSegment(sketch, "E28.6.18.0", {"start": v(-10.5, -28.1) * mm, "end": v(-10.78, -30.14) * mm});
            skLineSegment(sketch, "E28.9.18.0", {"start": v(-8.03, -28.9) * mm, "end": v(-9, -30.73) * mm});
            skLineSegment(sketch, "E28.1.19.0", {"start": v(-4.08, -31.75) * mm, "end": v(-5, -31.6) * mm});
            skLineSegment(sketch, "E28.3.19.0", {"start": v(-5.94, -31.46) * mm, "end": v(-5, -31.6) * mm});
            skLineSegment(sketch, "E28.6.19.0", {"start": v(-5.97, -29.4) * mm, "end": v(-5.94, -31.46) * mm});
            skLineSegment(sketch, "E28.9.19.0", {"start": v(-3.4, -29.8) * mm, "end": v(-4.08, -31.75) * mm});
            skLineSegment(sketch, "E28.1.20.0", {"start": v(0.94, -32) * mm, "end": v(0, -32) * mm});
            skLineSegment(sketch, "E28.3.20.0", {"start": v(-0.94, -32) * mm, "end": v(0, -32) * mm});
            skLineSegment(sketch, "E28.6.20.0", {"start": v(-1.3, -29.97) * mm, "end": v(-0.94, -32) * mm});
            skLineSegment(sketch, "E28.9.20.0", {"start": v(1.3, -29.97) * mm, "end": v(0.94, -32) * mm});
            skLineSegment(sketch, "E28.1.21.0", {"start": v(5.94, -31.46) * mm, "end": v(5, -31.6) * mm});
            skLineSegment(sketch, "E28.3.21.0", {"start": v(4.08, -31.75) * mm, "end": v(5, -31.6) * mm});
            skLineSegment(sketch, "E28.6.21.0", {"start": v(3.4, -29.8) * mm, "end": v(4.08, -31.75) * mm});
            skLineSegment(sketch, "E28.9.21.0", {"start": v(5.97, -29.4) * mm, "end": v(5.94, -31.46) * mm});
            skLineSegment(sketch, "E28.1.22.0", {"start": v(10.78, -30.14) * mm, "end": v(9.89, -30.43) * mm});
            skLineSegment(sketch, "E28.3.22.0", {"start": v(9, -30.73) * mm, "end": v(9.89, -30.43) * mm});
            skLineSegment(sketch, "E28.6.22.0", {"start": v(8.03, -28.9) * mm, "end": v(9, -30.73) * mm});
            skLineSegment(sketch, "E28.9.22.0", {"start": v(10.5, -28.1) * mm, "end": v(10.78, -30.14) * mm});
            skLineSegment(sketch, "E28.1.23.0", {"start": v(15.37, -28.08) * mm, "end": v(14.53, -28.51) * mm});
            skLineSegment(sketch, "E28.3.23.0", {"start": v(13.69, -28.94) * mm, "end": v(14.53, -28.51) * mm});
            skLineSegment(sketch, "E28.6.23.0", {"start": v(12.45, -27.3) * mm, "end": v(13.69, -28.94) * mm});
            skLineSegment(sketch, "E28.9.23.0", {"start": v(14.77, -26.11) * mm, "end": v(15.37, -28.08) * mm});
            skLineSegment(sketch, "E28.1.24.0", {"start": v(19.57, -25.33) * mm, "end": v(18.8, -25.89) * mm});
            skLineSegment(sketch, "E28.3.24.0", {"start": v(18.05, -26.44) * mm, "end": v(18.8, -25.89) * mm});
            skLineSegment(sketch, "E28.6.24.0", {"start": v(16.57, -25.01) * mm, "end": v(18.05, -26.44) * mm});
            skLineSegment(sketch, "E28.9.24.0", {"start": v(18.67, -23.48) * mm, "end": v(19.57, -25.33) * mm});
            skLineSegment(sketch, "E28.1.25.0", {"start": v(23.3, -21.96) * mm, "end": v(22.63, -22.63) * mm});
            skLineSegment(sketch, "E28.3.25.0", {"start": v(21.96, -23.3) * mm, "end": v(22.63, -22.63) * mm});
            skLineSegment(sketch, "E28.6.25.0", {"start": v(20.27, -22.11) * mm, "end": v(21.96, -23.3) * mm});
            skLineSegment(sketch, "E28.9.25.0", {"start": v(22.11, -20.27) * mm, "end": v(23.3, -21.96) * mm});
            skLineSegment(sketch, "E28.1.26.0", {"start": v(26.44, -18.05) * mm, "end": v(25.89, -18.8) * mm});
            skLineSegment(sketch, "E28.3.26.0", {"start": v(25.33, -19.57) * mm, "end": v(25.89, -18.8) * mm});
            skLineSegment(sketch, "E28.6.26.0", {"start": v(23.48, -18.67) * mm, "end": v(25.33, -19.57) * mm});
            skLineSegment(sketch, "E28.9.26.0", {"start": v(25.01, -16.57) * mm, "end": v(26.44, -18.05) * mm});
            skLineSegment(sketch, "E28.1.27.0", {"start": v(28.94, -13.69) * mm, "end": v(28.51, -14.53) * mm});
            skLineSegment(sketch, "E28.3.27.0", {"start": v(28.08, -15.37) * mm, "end": v(28.51, -14.53) * mm});
            skLineSegment(sketch, "E28.6.27.0", {"start": v(26.11, -14.77) * mm, "end": v(28.08, -15.37) * mm});
            skLineSegment(sketch, "E28.9.27.0", {"start": v(27.3, -12.45) * mm, "end": v(28.94, -13.69) * mm});
            skLineSegment(sketch, "E28.1.28.0", {"start": v(30.73, -9) * mm, "end": v(30.43, -9.89) * mm});
            skLineSegment(sketch, "E28.3.28.0", {"start": v(30.14, -10.78) * mm, "end": v(30.43, -9.89) * mm});
            skLineSegment(sketch, "E28.6.28.0", {"start": v(28.1, -10.5) * mm, "end": v(30.14, -10.78) * mm});
            skLineSegment(sketch, "E28.9.28.0", {"start": v(28.9, -8.03) * mm, "end": v(30.73, -9) * mm});
            skLineSegment(sketch, "E28.1.29.0", {"start": v(31.75, -4.08) * mm, "end": v(31.6, -5) * mm});
            skLineSegment(sketch, "E28.3.29.0", {"start": v(31.46, -5.94) * mm, "end": v(31.6, -5) * mm});
            skLineSegment(sketch, "E28.6.29.0", {"start": v(29.4, -5.97) * mm, "end": v(31.46, -5.94) * mm});
            skLineSegment(sketch, "E28.9.29.0", {"start": v(29.8, -3.4) * mm, "end": v(31.75, -4.08) * mm});
            skLineSegment(sketch, "E28.1.30.0", {"start": v(32, 0.94) * mm, "end": v(32, 0) * mm});
            skLineSegment(sketch, "E28.3.30.0", {"start": v(32, -0.94) * mm, "end": v(32, 0) * mm});
            skLineSegment(sketch, "E28.6.30.0", {"start": v(29.97, -1.3) * mm, "end": v(32, -0.94) * mm});
            skLineSegment(sketch, "E28.9.30.0", {"start": v(29.97, 1.3) * mm, "end": v(32, 0.94) * mm});
            skLineSegment(sketch, "E28.1.31.0", {"start": v(31.46, 5.94) * mm, "end": v(31.6, 5) * mm});
            skLineSegment(sketch, "E28.3.31.0", {"start": v(31.75, 4.08) * mm, "end": v(31.6, 5) * mm});
            skLineSegment(sketch, "E28.6.31.0", {"start": v(29.8, 3.4) * mm, "end": v(31.75, 4.08) * mm});
            skLineSegment(sketch, "E28.9.31.0", {"start": v(29.4, 5.97) * mm, "end": v(31.46, 5.94) * mm});
            skLineSegment(sketch, "E28.1.32.0", {"start": v(30.14, 10.78) * mm, "end": v(30.43, 9.89) * mm});
            skLineSegment(sketch, "E28.3.32.0", {"start": v(30.73, 9) * mm, "end": v(30.43, 9.89) * mm});
            skLineSegment(sketch, "E28.6.32.0", {"start": v(28.9, 8.03) * mm, "end": v(30.73, 9) * mm});
            skLineSegment(sketch, "E28.9.32.0", {"start": v(28.1, 10.5) * mm, "end": v(30.14, 10.78) * mm});
            skLineSegment(sketch, "E28.1.33.0", {"start": v(28.08, 15.37) * mm, "end": v(28.51, 14.53) * mm});
            skLineSegment(sketch, "E28.3.33.0", {"start": v(28.94, 13.69) * mm, "end": v(28.51, 14.53) * mm});
            skLineSegment(sketch, "E28.6.33.0", {"start": v(27.3, 12.45) * mm, "end": v(28.94, 13.69) * mm});
            skLineSegment(sketch, "E28.9.33.0", {"start": v(26.11, 14.77) * mm, "end": v(28.08, 15.37) * mm});
            skLineSegment(sketch, "E28.1.34.0", {"start": v(25.33, 19.57) * mm, "end": v(25.89, 18.8) * mm});
            skLineSegment(sketch, "E28.3.34.0", {"start": v(26.44, 18.05) * mm, "end": v(25.89, 18.8) * mm});
            skLineSegment(sketch, "E28.6.34.0", {"start": v(25.01, 16.57) * mm, "end": v(26.44, 18.05) * mm});
            skLineSegment(sketch, "E28.9.34.0", {"start": v(23.48, 18.67) * mm, "end": v(25.33, 19.57) * mm});
            skLineSegment(sketch, "E28.1.35.0", {"start": v(21.96, 23.3) * mm, "end": v(22.63, 22.63) * mm});
            skLineSegment(sketch, "E28.3.35.0", {"start": v(23.3, 21.96) * mm, "end": v(22.63, 22.63) * mm});
            skLineSegment(sketch, "E28.6.35.0", {"start": v(22.11, 20.27) * mm, "end": v(23.3, 21.96) * mm});
            skLineSegment(sketch, "E28.9.35.0", {"start": v(20.27, 22.11) * mm, "end": v(21.96, 23.3) * mm});
            skLineSegment(sketch, "E28.1.36.0", {"start": v(18.05, 26.44) * mm, "end": v(18.8, 25.89) * mm});
            skLineSegment(sketch, "E28.3.36.0", {"start": v(19.57, 25.33) * mm, "end": v(18.8, 25.89) * mm});
            skLineSegment(sketch, "E28.6.36.0", {"start": v(18.67, 23.48) * mm, "end": v(19.57, 25.33) * mm});
            skLineSegment(sketch, "E28.9.36.0", {"start": v(16.57, 25.01) * mm, "end": v(18.05, 26.44) * mm});
            skLineSegment(sketch, "E28.1.37.0", {"start": v(13.69, 28.94) * mm, "end": v(14.53, 28.51) * mm});
            skLineSegment(sketch, "E28.3.37.0", {"start": v(15.37, 28.08) * mm, "end": v(14.53, 28.51) * mm});
            skLineSegment(sketch, "E28.6.37.0", {"start": v(14.77, 26.11) * mm, "end": v(15.37, 28.08) * mm});
            skLineSegment(sketch, "E28.9.37.0", {"start": v(12.45, 27.3) * mm, "end": v(13.69, 28.94) * mm});
            skLineSegment(sketch, "E28.1.38.0", {"start": v(9, 30.73) * mm, "end": v(9.89, 30.43) * mm});
            skLineSegment(sketch, "E28.3.38.0", {"start": v(10.78, 30.14) * mm, "end": v(9.89, 30.43) * mm});
            skLineSegment(sketch, "E28.6.38.0", {"start": v(10.5, 28.1) * mm, "end": v(10.78, 30.14) * mm});
            skLineSegment(sketch, "E28.9.38.0", {"start": v(8.03, 28.9) * mm, "end": v(9, 30.73) * mm});
            skLineSegment(sketch, "E28.1.39.0", {"start": v(4.08, 31.75) * mm, "end": v(5, 31.6) * mm});
            skLineSegment(sketch, "E28.3.39.0", {"start": v(5.94, 31.46) * mm, "end": v(5, 31.6) * mm});
            skLineSegment(sketch, "E28.6.39.0", {"start": v(5.97, 29.4) * mm, "end": v(5.94, 31.46) * mm});
            skLineSegment(sketch, "E28.9.39.0", {"start": v(3.4, 29.8) * mm, "end": v(4.08, 31.75) * mm});
            skSolve(sketch);
        }
        {
            var Q0;
            Q0 = qSketchRegion(id + "F14", true);
            extrude(context, id + "F15", {"entities" : qUnion([Q0]), "operationType" : NewBodyOperationType.ADD, "depth" : 4 * mm, "offsetDistance" : 25 * mm});
        }
        {
            var Q0;
            Q0=makeQuery(id+"F7.opExtrude","CAP_FACE",FACE,{"disambiguationData":[OSD([sQuery(id+"F0.wireOp",EDGE,"E0")])],"isStart":false});
            var sketch = newSketch(context, id + "F16", { "sketchPlane" : qUnion([Q0])});
            skCircle(sketch, "E29", {"center": v(40, 0) * mm, "radius": 7.5 * mm});
            skLineSegment(sketch, "E30", {"start": v(40, 0) * mm, "end": v(40, 7.5) * mm, "construction": true});
            skLineSegment(sketch, "E31", {"start": v(38.68, 7.38) * mm, "end": v(39.06, 9.5) * mm});
            skLineSegment(sketch, "E32", {"start": v(39.06, 9.5) * mm, "end": v(40.94, 9.5) * mm});
            skLineSegment(sketch, "E33.MirrorCS", {"start": v(41.32, 7.38) * mm, "end": v(40.94, 9.5) * mm});
            skLineSegment(sketch, "E34.1.0", {"start": v(33.65, 7.13) * mm, "end": v(35.18, 8.24) * mm});
            skLineSegment(sketch, "E34.1.1", {"start": v(34.6, 5.2) * mm, "end": v(33.65, 7.13) * mm});
            skLineSegment(sketch, "E34.1.2", {"start": v(36.72, 6.75) * mm, "end": v(35.18, 8.24) * mm});
            skLineSegment(sketch, "E34.2.0", {"start": v(30.67, 2.04) * mm, "end": v(31.26, 3.83) * mm});
            skLineSegment(sketch, "E34.2.1", {"start": v(32.57, 1.03) * mm, "end": v(30.67, 2.04) * mm});
            skLineSegment(sketch, "E34.2.2", {"start": v(33.38, 3.53) * mm, "end": v(31.26, 3.83) * mm});
            skLineSegment(sketch, "E35.1.3.0", {"start": v(31.26, -3.83) * mm, "end": v(30.67, -2.04) * mm});
            skLineSegment(sketch, "E35.3.3.0", {"start": v(33.38, -3.53) * mm, "end": v(31.26, -3.83) * mm});
            skLineSegment(sketch, "E35.6.3.0", {"start": v(32.57, -1.03) * mm, "end": v(30.67, -2.04) * mm});
            skLineSegment(sketch, "E35.1.4.0", {"start": v(35.18, -8.24) * mm, "end": v(33.65, -7.13) * mm});
            skLineSegment(sketch, "E35.3.4.0", {"start": v(36.72, -6.75) * mm, "end": v(35.18, -8.24) * mm});
            skLineSegment(sketch, "E35.6.4.0", {"start": v(34.6, -5.2) * mm, "end": v(33.65, -7.13) * mm});
            skLineSegment(sketch, "E35.1.5.0", {"start": v(40.94, -9.5) * mm, "end": v(39.06, -9.5) * mm});
            skLineSegment(sketch, "E35.3.5.0", {"start": v(41.32, -7.38) * mm, "end": v(40.94, -9.5) * mm});
            skLineSegment(sketch, "E35.6.5.0", {"start": v(38.68, -7.38) * mm, "end": v(39.06, -9.5) * mm});
            skLineSegment(sketch, "E35.1.6.0", {"start": v(46.35, -7.13) * mm, "end": v(44.82, -8.24) * mm});
            skLineSegment(sketch, "E35.3.6.0", {"start": v(45.4, -5.2) * mm, "end": v(46.35, -7.13) * mm});
            skLineSegment(sketch, "E35.6.6.0", {"start": v(43.28, -6.75) * mm, "end": v(44.82, -8.24) * mm});
            skLineSegment(sketch, "E35.1.7.0", {"start": v(49.33, -2.04) * mm, "end": v(48.74, -3.83) * mm});
            skLineSegment(sketch, "E35.3.7.0", {"start": v(47.43, -1.03) * mm, "end": v(49.33, -2.04) * mm});
            skLineSegment(sketch, "E35.6.7.0", {"start": v(46.62, -3.53) * mm, "end": v(48.74, -3.83) * mm});
            skLineSegment(sketch, "E35.1.8.0", {"start": v(48.74, 3.83) * mm, "end": v(49.33, 2.04) * mm});
            skLineSegment(sketch, "E35.3.8.0", {"start": v(46.62, 3.53) * mm, "end": v(48.74, 3.83) * mm});
            skLineSegment(sketch, "E35.6.8.0", {"start": v(47.43, 1.03) * mm, "end": v(49.33, 2.04) * mm});
            skLineSegment(sketch, "E35.1.9.0", {"start": v(44.82, 8.24) * mm, "end": v(46.35, 7.13) * mm});
            skLineSegment(sketch, "E35.3.9.0", {"start": v(43.28, 6.75) * mm, "end": v(44.82, 8.24) * mm});
            skLineSegment(sketch, "E35.6.9.0", {"start": v(45.4, 5.2) * mm, "end": v(46.35, 7.13) * mm});
            skSolve(sketch);
        }
        {
            var Q0;
            Q0 = qSketchRegion(id + "F16", true);
            extrude(context, id + "F17", {"entities" : qUnion([Q0]), "operationType" : NewBodyOperationType.ADD, "depth" : 4 * mm, "offsetDistance" : 25 * mm});
        }
        {
            var Q0;
            Q0=makeQuery(id+"F17.opExtrude","CAP_FACE",FACE,{"disambiguationData":[OSD([sQuery(id+"F16.wireOp",EDGE,"E29"),sQuery(id+"F16.wireOp",EDGE,"E31"),sQuery(id+"F16.wireOp",EDGE,"E32"),sQuery(id+"F16.wireOp",EDGE,"E33.MirrorCS"),sQuery(id+"F16.wireOp",EDGE,"E34.1.0"),sQuery(id+"F16.wireOp",EDGE,"E34.1.1"),sQuery(id+"F16.wireOp",EDGE,"E34.1.2"),sQuery(id+"F16.wireOp",EDGE,"E34.2.0"),sQuery(id+"F16.wireOp",EDGE,"E34.2.1"),sQuery(id+"F16.wireOp",EDGE,"E34.2.2"),sQuery(id+"F16.wireOp",EDGE,"E35.1.3.0"),sQuery(id+"F16.wireOp",EDGE,"E35.3.3.0"),sQuery(id+"F16.wireOp",EDGE,"E35.6.3.0"),sQuery(id+"F16.wireOp",EDGE,"E35.1.4.0"),sQuery(id+"F16.wireOp",EDGE,"E35.3.4.0"),sQuery(id+"F16.wireOp",EDGE,"E35.6.4.0"),sQuery(id+"F16.wireOp",EDGE,"E35.1.5.0"),sQuery(id+"F16.wireOp",EDGE,"E35.3.5.0"),sQuery(id+"F16.wireOp",EDGE,"E35.6.5.0"),sQuery(id+"F16.wireOp",EDGE,"E35.1.6.0"),sQuery(id+"F16.wireOp",EDGE,"E35.3.6.0"),sQuery(id+"F16.wireOp",EDGE,"E35.6.6.0"),sQuery(id+"F16.wireOp",EDGE,"E35.1.7.0"),sQuery(id+"F16.wireOp",EDGE,"E35.3.7.0"),sQuery(id+"F16.wireOp",EDGE,"E35.6.7.0"),sQuery(id+"F16.wireOp",EDGE,"E35.1.8.0"),sQuery(id+"F16.wireOp",EDGE,"E35.3.8.0"),sQuery(id+"F16.wireOp",EDGE,"E35.6.8.0"),sQuery(id+"F16.wireOp",EDGE,"E35.1.9.0"),sQuery(id+"F16.wireOp",EDGE,"E35.3.9.0"),sQuery(id+"F16.wireOp",EDGE,"E35.6.9.0")])],"isStart":false});
            var sketch = newSketch(context, id + "F18", { "sketchPlane" : qUnion([Q0])});
            skCircle(sketch, "E36.0", {"center": v(40, 0) * mm, "radius": 3 * mm});
            skSolve(sketch);
        }
        {
            var Q0;
            Q0 = qSketchRegion(id + "F18", true);
            extrude(context, id + "F19", {"entities" : qUnion([Q0]), "operationType" : NewBodyOperationType.ADD, "depth" : 2 * mm, "offsetDistance" : 25 * mm});
        }
        {
            var Q0;
            Q0=makeQuery(id+"F19.opExtrude","CAP_FACE",FACE,{"disambiguationData":[OSD([sQuery(id+"F18.wireOp",EDGE,"E36.0")])],"isStart":false});
            var sketch = newSketch(context, id + "F20", { "sketchPlane" : qUnion([Q0])});
            skCircle(sketch, "E37", {"center": v(0, 0) * mm, "radius": 98 * mm});
            skCircle(sketch, "E38.0", {"center": v(0, 0) * mm, "radius": 5 * mm});
            skSolve(sketch);
        }
        {
            var Q0;
            Q0 = qSketchRegion(id + "F20", true);
            extrude(context, id + "F21", {"entities" : qUnion([Q0]), "depth" : 1 * mm, "offsetDistance" : 25 * mm});
        }
        {
            var Q0;
            Q0=makeQuery(id+"F21.opExtrude","SWEPT_BODY",BODY,{"disambiguationData":[OSD([sQuery(id+"F20.wireOp",EDGE,"E37"),sQuery(id+"F20.wireOp",EDGE,"E38.0")])]});
            var Q1;
            Q1=makeQuery(id+"F1.opExtrude","SWEPT_BODY",BODY,{"disambiguationData":[OSD([sQuery(id+"F0.wireOp",EDGE,"E0")])]});
            booleanBodies(context, id + "F22", {"operationType" : BooleanOperationType.SUBTRACTION, "tools" : qUnion([Q0]), "targets" : qUnion([Q1]), "keepTools" : true});
        }
        {
            var Q0;
            Q0=makeQuery(id+"F21.opExtrude","CAP_FACE",FACE,{"disambiguationData":[OSD([sQuery(id+"F20.wireOp",EDGE,"E37"),sQuery(id+"F20.wireOp",EDGE,"E38.0")])],"isStart":true});
            var sketch = newSketch(context, id + "F23", { "sketchPlane" : qUnion([Q0])});
            skCircle(sketch, "E39.0", {"center": v(-40, 0) * mm, "radius": 3 * mm});
            skCircle(sketch, "E40", {"center": v(-40, 0) * mm, "radius": 5 * mm});
            skSolve(sketch);
        }
        {
            var Q0;
            Q0 = qSketchRegion(id + "F23", true);
            extrude(context, id + "F24", {"entities" : qUnion([Q0]), "operationType" : NewBodyOperationType.ADD, "endBound" : BoundingType.UP_TO_NEXT, "depth" : 25 * mm, "offsetDistance" : 25 * mm});
        }
        {
            var Q0;
            Q0=makeQuery(id+"F21.opExtrude","CAP_FACE",FACE,{"disambiguationData":[OSD([sQuery(id+"F20.wireOp",EDGE,"E37"),sQuery(id+"F20.wireOp",EDGE,"E38.0")])],"isStart":false});
            var sketch = newSketch(context, id + "F25", { "sketchPlane" : qUnion([Q0])});
            skLineSegment(sketch, "E41.bottom", {"start": v(1.5, 71) * mm, "end": v(-1.5, 71) * mm});
            skLineSegment(sketch, "E41.top", {"start": v(1.5, 91) * mm, "end": v(-1.5, 91) * mm});
            skLineSegment(sketch, "E41.left", {"start": v(1.5, 71) * mm, "end": v(1.5, 91) * mm});
            skLineSegment(sketch, "E41.right", {"start": v(-1.5, 71) * mm, "end": v(-1.5, 91) * mm});
            skPoint(sketch, "E41.middle", {"position": v(0, 81) * mm});
            skLineSegment(sketch, "E42.1.0", {"start": v(-34.2, 62.24) * mm, "end": v(-44.2, 79.56) * mm});
            skLineSegment(sketch, "E42.1.1", {"start": v(-36.8, 60.74) * mm, "end": v(-46.8, 78.06) * mm});
            skLineSegment(sketch, "E42.1.2", {"start": v(-44.2, 79.56) * mm, "end": v(-46.8, 78.06) * mm});
            skLineSegment(sketch, "E42.1.3", {"start": v(-34.2, 62.24) * mm, "end": v(-36.8, 60.74) * mm});
            skLineSegment(sketch, "E42.2.0", {"start": v(-60.74, 36.8) * mm, "end": v(-78.06, 46.8) * mm});
            skLineSegment(sketch, "E42.2.1", {"start": v(-62.24, 34.2) * mm, "end": v(-79.56, 44.2) * mm});
            skLineSegment(sketch, "E42.2.2", {"start": v(-78.06, 46.8) * mm, "end": v(-79.56, 44.2) * mm});
            skLineSegment(sketch, "E42.2.3", {"start": v(-60.74, 36.8) * mm, "end": v(-62.24, 34.2) * mm});
            skPoint(sketch, "E42.center", {"position": v(0, 0) * mm});
            skLineSegment(sketch, "E43.1.3.0", {"start": v(-71, 1.5) * mm, "end": v(-91, 1.5) * mm});
            skLineSegment(sketch, "E43.3.3.0", {"start": v(-71, -1.5) * mm, "end": v(-91, -1.5) * mm});
            skLineSegment(sketch, "E43.6.3.0", {"start": v(-91, 1.5) * mm, "end": v(-91, -1.5) * mm});
            skLineSegment(sketch, "E43.9.3.0", {"start": v(-71, 1.5) * mm, "end": v(-71, -1.5) * mm});
            skLineSegment(sketch, "E43.1.4.0", {"start": v(-62.24, -34.2) * mm, "end": v(-79.56, -44.2) * mm});
            skLineSegment(sketch, "E43.3.4.0", {"start": v(-60.74, -36.8) * mm, "end": v(-78.06, -46.8) * mm});
            skLineSegment(sketch, "E43.6.4.0", {"start": v(-79.56, -44.2) * mm, "end": v(-78.06, -46.8) * mm});
            skLineSegment(sketch, "E43.9.4.0", {"start": v(-62.24, -34.2) * mm, "end": v(-60.74, -36.8) * mm});
            skLineSegment(sketch, "E43.1.5.0", {"start": v(-36.8, -60.74) * mm, "end": v(-46.8, -78.06) * mm});
            skLineSegment(sketch, "E43.3.5.0", {"start": v(-34.2, -62.24) * mm, "end": v(-44.2, -79.56) * mm});
            skLineSegment(sketch, "E43.6.5.0", {"start": v(-46.8, -78.06) * mm, "end": v(-44.2, -79.56) * mm});
            skLineSegment(sketch, "E43.9.5.0", {"start": v(-36.8, -60.74) * mm, "end": v(-34.2, -62.24) * mm});
            skLineSegment(sketch, "E43.1.6.0", {"start": v(-1.5, -71) * mm, "end": v(-1.5, -91) * mm});
            skLineSegment(sketch, "E43.3.6.0", {"start": v(1.5, -71) * mm, "end": v(1.5, -91) * mm});
            skLineSegment(sketch, "E43.6.6.0", {"start": v(-1.5, -91) * mm, "end": v(1.5, -91) * mm});
            skLineSegment(sketch, "E43.9.6.0", {"start": v(-1.5, -71) * mm, "end": v(1.5, -71) * mm});
            skLineSegment(sketch, "E43.1.7.0", {"start": v(34.2, -62.24) * mm, "end": v(44.2, -79.56) * mm});
            skLineSegment(sketch, "E43.3.7.0", {"start": v(36.8, -60.74) * mm, "end": v(46.8, -78.06) * mm});
            skLineSegment(sketch, "E43.6.7.0", {"start": v(44.2, -79.56) * mm, "end": v(46.8, -78.06) * mm});
            skLineSegment(sketch, "E43.9.7.0", {"start": v(34.2, -62.24) * mm, "end": v(36.8, -60.74) * mm});
            skLineSegment(sketch, "E43.1.8.0", {"start": v(60.74, -36.8) * mm, "end": v(78.06, -46.8) * mm});
            skLineSegment(sketch, "E43.3.8.0", {"start": v(62.24, -34.2) * mm, "end": v(79.56, -44.2) * mm});
            skLineSegment(sketch, "E43.6.8.0", {"start": v(78.06, -46.8) * mm, "end": v(79.56, -44.2) * mm});
            skLineSegment(sketch, "E43.9.8.0", {"start": v(60.74, -36.8) * mm, "end": v(62.24, -34.2) * mm});
            skLineSegment(sketch, "E43.1.9.0", {"start": v(71, -1.5) * mm, "end": v(91, -1.5) * mm});
            skLineSegment(sketch, "E43.3.9.0", {"start": v(71, 1.5) * mm, "end": v(91, 1.5) * mm});
            skLineSegment(sketch, "E43.6.9.0", {"start": v(91, -1.5) * mm, "end": v(91, 1.5) * mm});
            skLineSegment(sketch, "E43.9.9.0", {"start": v(71, -1.5) * mm, "end": v(71, 1.5) * mm});
            skLineSegment(sketch, "E43.1.10.0", {"start": v(62.24, 34.2) * mm, "end": v(79.56, 44.2) * mm});
            skLineSegment(sketch, "E43.3.10.0", {"start": v(60.74, 36.8) * mm, "end": v(78.06, 46.8) * mm});
            skLineSegment(sketch, "E43.6.10.0", {"start": v(79.56, 44.2) * mm, "end": v(78.06, 46.8) * mm});
            skLineSegment(sketch, "E43.9.10.0", {"start": v(62.24, 34.2) * mm, "end": v(60.74, 36.8) * mm});
            skLineSegment(sketch, "E43.1.11.0", {"start": v(36.8, 60.74) * mm, "end": v(46.8, 78.06) * mm});
            skLineSegment(sketch, "E43.3.11.0", {"start": v(34.2, 62.24) * mm, "end": v(44.2, 79.56) * mm});
            skLineSegment(sketch, "E43.6.11.0", {"start": v(46.8, 78.06) * mm, "end": v(44.2, 79.56) * mm});
            skLineSegment(sketch, "E43.9.11.0", {"start": v(36.8, 60.74) * mm, "end": v(34.2, 62.24) * mm});
            skSolve(sketch);
        }
        {
            var Q0;
            Q0 = qSketchRegion(id + "F25", true);
            extrude(context, id + "F26", {"entities" : qUnion([Q0]), "operationType" : NewBodyOperationType.REMOVE, "oppositeDirection" : true, "depth" : 0.5 * mm, "offsetDistance" : 25 * mm});
        }
        {
            var Q0;
            Q0=makeQuery(id+"F21.opExtrude","CAP_FACE",FACE,{"disambiguationData":[OSD([sQuery(id+"F20.wireOp",EDGE,"E37"),sQuery(id+"F20.wireOp",EDGE,"E38.0")])],"isStart":false});
            var sketch = newSketch(context, id + "F27", { "sketchPlane" : qUnion([Q0])});
            skLineSegment(sketch, "E44.bottom", {"start": v(0.75, 78.5) * mm, "end": v(-0.75, 78.5) * mm});
            skLineSegment(sketch, "E44.top", {"start": v(0.75, 90.5) * mm, "end": v(-0.75, 90.5) * mm});
            skLineSegment(sketch, "E44.left", {"start": v(0.75, 78.5) * mm, "end": v(0.75, 90.5) * mm});
            skLineSegment(sketch, "E44.right", {"start": v(-0.75, 78.5) * mm, "end": v(-0.75, 90.5) * mm});
            skPoint(sketch, "E44.middle", {"position": v(0, 84.5) * mm});
            skLineSegment(sketch, "E45.1.0", {"start": v(-8.71, 90.08) * mm, "end": v(-10.2, 89.93) * mm});
            skLineSegment(sketch, "E45.1.1", {"start": v(-8.95, 78) * mm, "end": v(-10.2, 89.93) * mm});
            skLineSegment(sketch, "E45.1.2", {"start": v(-7.46, 78.15) * mm, "end": v(-8.71, 90.08) * mm});
            skLineSegment(sketch, "E45.1.3", {"start": v(-7.46, 78.15) * mm, "end": v(-8.95, 78) * mm});
            skLineSegment(sketch, "E45.2.0", {"start": v(-18.08, 88.68) * mm, "end": v(-19.55, 88.37) * mm});
            skLineSegment(sketch, "E45.2.1", {"start": v(-17.05, 76.63) * mm, "end": v(-19.55, 88.37) * mm});
            skLineSegment(sketch, "E45.2.2", {"start": v(-15.59, 76.94) * mm, "end": v(-18.08, 88.68) * mm});
            skLineSegment(sketch, "E45.2.3", {"start": v(-15.59, 76.94) * mm, "end": v(-17.05, 76.63) * mm});
            skPoint(sketch, "E45.center", {"position": v(0, 0) * mm});
            skLineSegment(sketch, "E46.2.3.0", {"start": v(-27.25, 86.3) * mm, "end": v(-28.68, 85.84) * mm});
            skLineSegment(sketch, "E46.3.3.0", {"start": v(-24.97, 74.43) * mm, "end": v(-28.68, 85.84) * mm});
            skLineSegment(sketch, "E46.6.3.0", {"start": v(-23.54, 74.89) * mm, "end": v(-27.25, 86.3) * mm});
            skLineSegment(sketch, "E46.9.3.0", {"start": v(-23.54, 74.89) * mm, "end": v(-24.97, 74.43) * mm});
            skLineSegment(sketch, "E46.2.4.0", {"start": v(-36.12, 82.98) * mm, "end": v(-37.5, 82.37) * mm});
            skLineSegment(sketch, "E46.3.4.0", {"start": v(-32.61, 71.4) * mm, "end": v(-37.5, 82.37) * mm});
            skLineSegment(sketch, "E46.6.4.0", {"start": v(-31.24, 72.02) * mm, "end": v(-36.12, 82.98) * mm});
            skLineSegment(sketch, "E46.9.4.0", {"start": v(-31.24, 72.02) * mm, "end": v(-32.61, 71.4) * mm});
            skLineSegment(sketch, "E46.2.5.0", {"start": v(-44.6, 78.75) * mm, "end": v(-45.9, 78) * mm});
            skLineSegment(sketch, "E46.3.5.0", {"start": v(-39.9, 67.6) * mm, "end": v(-45.9, 78) * mm});
            skLineSegment(sketch, "E46.6.5.0", {"start": v(-38.6, 68.36) * mm, "end": v(-44.6, 78.75) * mm});
            skLineSegment(sketch, "E46.9.5.0", {"start": v(-38.6, 68.36) * mm, "end": v(-39.9, 67.6) * mm});
            skLineSegment(sketch, "E46.2.6.0", {"start": v(-52.59, 73.66) * mm, "end": v(-53.8, 72.78) * mm});
            skLineSegment(sketch, "E46.3.6.0", {"start": v(-46.75, 63.07) * mm, "end": v(-53.8, 72.78) * mm});
            skLineSegment(sketch, "E46.6.6.0", {"start": v(-45.53, 63.95) * mm, "end": v(-52.59, 73.66) * mm});
            skLineSegment(sketch, "E46.9.6.0", {"start": v(-45.53, 63.95) * mm, "end": v(-46.75, 63.07) * mm});
            skLineSegment(sketch, "E46.2.7.0", {"start": v(-60, 67.76) * mm, "end": v(-61.11, 66.75) * mm});
            skLineSegment(sketch, "E46.3.7.0", {"start": v(-53.08, 57.84) * mm, "end": v(-61.11, 66.75) * mm});
            skLineSegment(sketch, "E46.6.7.0", {"start": v(-51.97, 58.84) * mm, "end": v(-60, 67.76) * mm});
            skLineSegment(sketch, "E46.9.7.0", {"start": v(-51.97, 58.84) * mm, "end": v(-53.08, 57.84) * mm});
            skLineSegment(sketch, "E46.2.8.0", {"start": v(-66.75, 61.11) * mm, "end": v(-67.76, 60) * mm});
            skLineSegment(sketch, "E46.3.8.0", {"start": v(-58.84, 51.97) * mm, "end": v(-67.76, 60) * mm});
            skLineSegment(sketch, "E46.6.8.0", {"start": v(-57.84, 53.08) * mm, "end": v(-66.75, 61.11) * mm});
            skLineSegment(sketch, "E46.9.8.0", {"start": v(-57.84, 53.08) * mm, "end": v(-58.84, 51.97) * mm});
            skLineSegment(sketch, "E46.2.9.0", {"start": v(-72.78, 53.8) * mm, "end": v(-73.66, 52.59) * mm});
            skLineSegment(sketch, "E46.3.9.0", {"start": v(-63.95, 45.53) * mm, "end": v(-73.66, 52.59) * mm});
            skLineSegment(sketch, "E46.6.9.0", {"start": v(-63.07, 46.75) * mm, "end": v(-72.78, 53.8) * mm});
            skLineSegment(sketch, "E46.9.9.0", {"start": v(-63.07, 46.75) * mm, "end": v(-63.95, 45.53) * mm});
            skLineSegment(sketch, "E46.2.10.0", {"start": v(-78, 45.9) * mm, "end": v(-78.75, 44.6) * mm});
            skLineSegment(sketch, "E46.3.10.0", {"start": v(-68.36, 38.6) * mm, "end": v(-78.75, 44.6) * mm});
            skLineSegment(sketch, "E46.6.10.0", {"start": v(-67.6, 39.9) * mm, "end": v(-78, 45.9) * mm});
            skLineSegment(sketch, "E46.9.10.0", {"start": v(-67.6, 39.9) * mm, "end": v(-68.36, 38.6) * mm});
            skLineSegment(sketch, "E46.2.11.0", {"start": v(-82.37, 37.5) * mm, "end": v(-82.98, 36.12) * mm});
            skLineSegment(sketch, "E46.3.11.0", {"start": v(-72.02, 31.24) * mm, "end": v(-82.98, 36.12) * mm});
            skLineSegment(sketch, "E46.6.11.0", {"start": v(-71.4, 32.61) * mm, "end": v(-82.37, 37.5) * mm});
            skLineSegment(sketch, "E46.9.11.0", {"start": v(-71.4, 32.61) * mm, "end": v(-72.02, 31.24) * mm});
            skLineSegment(sketch, "E46.2.12.0", {"start": v(-85.84, 28.68) * mm, "end": v(-86.3, 27.25) * mm});
            skLineSegment(sketch, "E46.3.12.0", {"start": v(-74.89, 23.54) * mm, "end": v(-86.3, 27.25) * mm});
            skLineSegment(sketch, "E46.6.12.0", {"start": v(-74.43, 24.97) * mm, "end": v(-85.84, 28.68) * mm});
            skLineSegment(sketch, "E46.9.12.0", {"start": v(-74.43, 24.97) * mm, "end": v(-74.89, 23.54) * mm});
            skLineSegment(sketch, "E46.2.13.0", {"start": v(-88.37, 19.55) * mm, "end": v(-88.68, 18.08) * mm});
            skLineSegment(sketch, "E46.3.13.0", {"start": v(-76.94, 15.59) * mm, "end": v(-88.68, 18.08) * mm});
            skLineSegment(sketch, "E46.6.13.0", {"start": v(-76.63, 17.05) * mm, "end": v(-88.37, 19.55) * mm});
            skLineSegment(sketch, "E46.9.13.0", {"start": v(-76.63, 17.05) * mm, "end": v(-76.94, 15.59) * mm});
            skLineSegment(sketch, "E46.2.14.0", {"start": v(-89.93, 10.2) * mm, "end": v(-90.08, 8.71) * mm});
            skLineSegment(sketch, "E46.3.14.0", {"start": v(-78.15, 7.46) * mm, "end": v(-90.08, 8.71) * mm});
            skLineSegment(sketch, "E46.6.14.0", {"start": v(-78, 8.95) * mm, "end": v(-89.93, 10.2) * mm});
            skLineSegment(sketch, "E46.9.14.0", {"start": v(-78, 8.95) * mm, "end": v(-78.15, 7.46) * mm});
            skLineSegment(sketch, "E46.2.15.0", {"start": v(-90.5, 0.75) * mm, "end": v(-90.5, -0.75) * mm});
            skLineSegment(sketch, "E46.3.15.0", {"start": v(-78.5, -0.75) * mm, "end": v(-90.5, -0.75) * mm});
            skLineSegment(sketch, "E46.6.15.0", {"start": v(-78.5, 0.75) * mm, "end": v(-90.5, 0.75) * mm});
            skLineSegment(sketch, "E46.9.15.0", {"start": v(-78.5, 0.75) * mm, "end": v(-78.5, -0.75) * mm});
            skLineSegment(sketch, "E46.2.16.0", {"start": v(-90.08, -8.71) * mm, "end": v(-89.93, -10.2) * mm});
            skLineSegment(sketch, "E46.3.16.0", {"start": v(-78, -8.95) * mm, "end": v(-89.93, -10.2) * mm});
            skLineSegment(sketch, "E46.6.16.0", {"start": v(-78.15, -7.46) * mm, "end": v(-90.08, -8.71) * mm});
            skLineSegment(sketch, "E46.9.16.0", {"start": v(-78.15, -7.46) * mm, "end": v(-78, -8.95) * mm});
            skLineSegment(sketch, "E46.2.17.0", {"start": v(-88.68, -18.08) * mm, "end": v(-88.37, -19.55) * mm});
            skLineSegment(sketch, "E46.3.17.0", {"start": v(-76.63, -17.05) * mm, "end": v(-88.37, -19.55) * mm});
            skLineSegment(sketch, "E46.6.17.0", {"start": v(-76.94, -15.59) * mm, "end": v(-88.68, -18.08) * mm});
            skLineSegment(sketch, "E46.9.17.0", {"start": v(-76.94, -15.59) * mm, "end": v(-76.63, -17.05) * mm});
            skLineSegment(sketch, "E46.2.18.0", {"start": v(-86.3, -27.25) * mm, "end": v(-85.84, -28.68) * mm});
            skLineSegment(sketch, "E46.3.18.0", {"start": v(-74.43, -24.97) * mm, "end": v(-85.84, -28.68) * mm});
            skLineSegment(sketch, "E46.6.18.0", {"start": v(-74.89, -23.54) * mm, "end": v(-86.3, -27.25) * mm});
            skLineSegment(sketch, "E46.9.18.0", {"start": v(-74.89, -23.54) * mm, "end": v(-74.43, -24.97) * mm});
            skLineSegment(sketch, "E46.2.19.0", {"start": v(-82.98, -36.12) * mm, "end": v(-82.37, -37.5) * mm});
            skLineSegment(sketch, "E46.3.19.0", {"start": v(-71.4, -32.61) * mm, "end": v(-82.37, -37.5) * mm});
            skLineSegment(sketch, "E46.6.19.0", {"start": v(-72.02, -31.24) * mm, "end": v(-82.98, -36.12) * mm});
            skLineSegment(sketch, "E46.9.19.0", {"start": v(-72.02, -31.24) * mm, "end": v(-71.4, -32.61) * mm});
            skLineSegment(sketch, "E46.2.20.0", {"start": v(-78.75, -44.6) * mm, "end": v(-78, -45.9) * mm});
            skLineSegment(sketch, "E46.3.20.0", {"start": v(-67.6, -39.9) * mm, "end": v(-78, -45.9) * mm});
            skLineSegment(sketch, "E46.6.20.0", {"start": v(-68.36, -38.6) * mm, "end": v(-78.75, -44.6) * mm});
            skLineSegment(sketch, "E46.9.20.0", {"start": v(-68.36, -38.6) * mm, "end": v(-67.6, -39.9) * mm});
            skLineSegment(sketch, "E46.2.21.0", {"start": v(-73.66, -52.59) * mm, "end": v(-72.78, -53.8) * mm});
            skLineSegment(sketch, "E46.3.21.0", {"start": v(-63.07, -46.75) * mm, "end": v(-72.78, -53.8) * mm});
            skLineSegment(sketch, "E46.6.21.0", {"start": v(-63.95, -45.53) * mm, "end": v(-73.66, -52.59) * mm});
            skLineSegment(sketch, "E46.9.21.0", {"start": v(-63.95, -45.53) * mm, "end": v(-63.07, -46.75) * mm});
            skLineSegment(sketch, "E46.2.22.0", {"start": v(-67.76, -60) * mm, "end": v(-66.75, -61.11) * mm});
            skLineSegment(sketch, "E46.3.22.0", {"start": v(-57.84, -53.08) * mm, "end": v(-66.75, -61.11) * mm});
            skLineSegment(sketch, "E46.6.22.0", {"start": v(-58.84, -51.97) * mm, "end": v(-67.76, -60) * mm});
            skLineSegment(sketch, "E46.9.22.0", {"start": v(-58.84, -51.97) * mm, "end": v(-57.84, -53.08) * mm});
            skLineSegment(sketch, "E46.2.23.0", {"start": v(-61.11, -66.75) * mm, "end": v(-60, -67.76) * mm});
            skLineSegment(sketch, "E46.3.23.0", {"start": v(-51.97, -58.84) * mm, "end": v(-60, -67.76) * mm});
            skLineSegment(sketch, "E46.6.23.0", {"start": v(-53.08, -57.84) * mm, "end": v(-61.11, -66.75) * mm});
            skLineSegment(sketch, "E46.9.23.0", {"start": v(-53.08, -57.84) * mm, "end": v(-51.97, -58.84) * mm});
            skLineSegment(sketch, "E46.2.24.0", {"start": v(-53.8, -72.78) * mm, "end": v(-52.59, -73.66) * mm});
            skLineSegment(sketch, "E46.3.24.0", {"start": v(-45.53, -63.95) * mm, "end": v(-52.59, -73.66) * mm});
            skLineSegment(sketch, "E46.6.24.0", {"start": v(-46.75, -63.07) * mm, "end": v(-53.8, -72.78) * mm});
            skLineSegment(sketch, "E46.9.24.0", {"start": v(-46.75, -63.07) * mm, "end": v(-45.53, -63.95) * mm});
            skLineSegment(sketch, "E46.2.25.0", {"start": v(-45.9, -78) * mm, "end": v(-44.6, -78.75) * mm});
            skLineSegment(sketch, "E46.3.25.0", {"start": v(-38.6, -68.36) * mm, "end": v(-44.6, -78.75) * mm});
            skLineSegment(sketch, "E46.6.25.0", {"start": v(-39.9, -67.6) * mm, "end": v(-45.9, -78) * mm});
            skLineSegment(sketch, "E46.9.25.0", {"start": v(-39.9, -67.6) * mm, "end": v(-38.6, -68.36) * mm});
            skLineSegment(sketch, "E46.2.26.0", {"start": v(-37.5, -82.37) * mm, "end": v(-36.12, -82.98) * mm});
            skLineSegment(sketch, "E46.3.26.0", {"start": v(-31.24, -72.02) * mm, "end": v(-36.12, -82.98) * mm});
            skLineSegment(sketch, "E46.6.26.0", {"start": v(-32.61, -71.4) * mm, "end": v(-37.5, -82.37) * mm});
            skLineSegment(sketch, "E46.9.26.0", {"start": v(-32.61, -71.4) * mm, "end": v(-31.24, -72.02) * mm});
            skLineSegment(sketch, "E46.2.27.0", {"start": v(-28.68, -85.84) * mm, "end": v(-27.25, -86.3) * mm});
            skLineSegment(sketch, "E46.3.27.0", {"start": v(-23.54, -74.89) * mm, "end": v(-27.25, -86.3) * mm});
            skLineSegment(sketch, "E46.6.27.0", {"start": v(-24.97, -74.43) * mm, "end": v(-28.68, -85.84) * mm});
            skLineSegment(sketch, "E46.9.27.0", {"start": v(-24.97, -74.43) * mm, "end": v(-23.54, -74.89) * mm});
            skLineSegment(sketch, "E46.2.28.0", {"start": v(-19.55, -88.37) * mm, "end": v(-18.08, -88.68) * mm});
            skLineSegment(sketch, "E46.3.28.0", {"start": v(-15.59, -76.94) * mm, "end": v(-18.08, -88.68) * mm});
            skLineSegment(sketch, "E46.6.28.0", {"start": v(-17.05, -76.63) * mm, "end": v(-19.55, -88.37) * mm});
            skLineSegment(sketch, "E46.9.28.0", {"start": v(-17.05, -76.63) * mm, "end": v(-15.59, -76.94) * mm});
            skLineSegment(sketch, "E46.2.29.0", {"start": v(-10.2, -89.93) * mm, "end": v(-8.71, -90.08) * mm});
            skLineSegment(sketch, "E46.3.29.0", {"start": v(-7.46, -78.15) * mm, "end": v(-8.71, -90.08) * mm});
            skLineSegment(sketch, "E46.6.29.0", {"start": v(-8.95, -78) * mm, "end": v(-10.2, -89.93) * mm});
            skLineSegment(sketch, "E46.9.29.0", {"start": v(-8.95, -78) * mm, "end": v(-7.46, -78.15) * mm});
            skLineSegment(sketch, "E46.2.30.0", {"start": v(-0.75, -90.5) * mm, "end": v(0.75, -90.5) * mm});
            skLineSegment(sketch, "E46.3.30.0", {"start": v(0.75, -78.5) * mm, "end": v(0.75, -90.5) * mm});
            skLineSegment(sketch, "E46.6.30.0", {"start": v(-0.75, -78.5) * mm, "end": v(-0.75, -90.5) * mm});
            skLineSegment(sketch, "E46.9.30.0", {"start": v(-0.75, -78.5) * mm, "end": v(0.75, -78.5) * mm});
            skLineSegment(sketch, "E46.2.31.0", {"start": v(8.71, -90.08) * mm, "end": v(10.2, -89.93) * mm});
            skLineSegment(sketch, "E46.3.31.0", {"start": v(8.95, -78) * mm, "end": v(10.2, -89.93) * mm});
            skLineSegment(sketch, "E46.6.31.0", {"start": v(7.46, -78.15) * mm, "end": v(8.71, -90.08) * mm});
            skLineSegment(sketch, "E46.9.31.0", {"start": v(7.46, -78.15) * mm, "end": v(8.95, -78) * mm});
            skLineSegment(sketch, "E46.2.32.0", {"start": v(18.08, -88.68) * mm, "end": v(19.55, -88.37) * mm});
            skLineSegment(sketch, "E46.3.32.0", {"start": v(17.05, -76.63) * mm, "end": v(19.55, -88.37) * mm});
            skLineSegment(sketch, "E46.6.32.0", {"start": v(15.59, -76.94) * mm, "end": v(18.08, -88.68) * mm});
            skLineSegment(sketch, "E46.9.32.0", {"start": v(15.59, -76.94) * mm, "end": v(17.05, -76.63) * mm});
            skLineSegment(sketch, "E46.2.33.0", {"start": v(27.25, -86.3) * mm, "end": v(28.68, -85.84) * mm});
            skLineSegment(sketch, "E46.3.33.0", {"start": v(24.97, -74.43) * mm, "end": v(28.68, -85.84) * mm});
            skLineSegment(sketch, "E46.6.33.0", {"start": v(23.54, -74.89) * mm, "end": v(27.25, -86.3) * mm});
            skLineSegment(sketch, "E46.9.33.0", {"start": v(23.54, -74.89) * mm, "end": v(24.97, -74.43) * mm});
            skLineSegment(sketch, "E46.2.34.0", {"start": v(36.12, -82.98) * mm, "end": v(37.5, -82.37) * mm});
            skLineSegment(sketch, "E46.3.34.0", {"start": v(32.61, -71.4) * mm, "end": v(37.5, -82.37) * mm});
            skLineSegment(sketch, "E46.6.34.0", {"start": v(31.24, -72.02) * mm, "end": v(36.12, -82.98) * mm});
            skLineSegment(sketch, "E46.9.34.0", {"start": v(31.24, -72.02) * mm, "end": v(32.61, -71.4) * mm});
            skLineSegment(sketch, "E46.2.35.0", {"start": v(44.6, -78.75) * mm, "end": v(45.9, -78) * mm});
            skLineSegment(sketch, "E46.3.35.0", {"start": v(39.9, -67.6) * mm, "end": v(45.9, -78) * mm});
            skLineSegment(sketch, "E46.6.35.0", {"start": v(38.6, -68.36) * mm, "end": v(44.6, -78.75) * mm});
            skLineSegment(sketch, "E46.9.35.0", {"start": v(38.6, -68.36) * mm, "end": v(39.9, -67.6) * mm});
            skLineSegment(sketch, "E46.2.36.0", {"start": v(52.59, -73.66) * mm, "end": v(53.8, -72.78) * mm});
            skLineSegment(sketch, "E46.3.36.0", {"start": v(46.75, -63.07) * mm, "end": v(53.8, -72.78) * mm});
            skLineSegment(sketch, "E46.6.36.0", {"start": v(45.53, -63.95) * mm, "end": v(52.59, -73.66) * mm});
            skLineSegment(sketch, "E46.9.36.0", {"start": v(45.53, -63.95) * mm, "end": v(46.75, -63.07) * mm});
            skLineSegment(sketch, "E46.2.37.0", {"start": v(60, -67.76) * mm, "end": v(61.11, -66.75) * mm});
            skLineSegment(sketch, "E46.3.37.0", {"start": v(53.08, -57.84) * mm, "end": v(61.11, -66.75) * mm});
            skLineSegment(sketch, "E46.6.37.0", {"start": v(51.97, -58.84) * mm, "end": v(60, -67.76) * mm});
            skLineSegment(sketch, "E46.9.37.0", {"start": v(51.97, -58.84) * mm, "end": v(53.08, -57.84) * mm});
            skLineSegment(sketch, "E46.2.38.0", {"start": v(66.75, -61.11) * mm, "end": v(67.76, -60) * mm});
            skLineSegment(sketch, "E46.3.38.0", {"start": v(58.84, -51.97) * mm, "end": v(67.76, -60) * mm});
            skLineSegment(sketch, "E46.6.38.0", {"start": v(57.84, -53.08) * mm, "end": v(66.75, -61.11) * mm});
            skLineSegment(sketch, "E46.9.38.0", {"start": v(57.84, -53.08) * mm, "end": v(58.84, -51.97) * mm});
            skLineSegment(sketch, "E46.2.39.0", {"start": v(72.78, -53.8) * mm, "end": v(73.66, -52.59) * mm});
            skLineSegment(sketch, "E46.3.39.0", {"start": v(63.95, -45.53) * mm, "end": v(73.66, -52.59) * mm});
            skLineSegment(sketch, "E46.6.39.0", {"start": v(63.07, -46.75) * mm, "end": v(72.78, -53.8) * mm});
            skLineSegment(sketch, "E46.9.39.0", {"start": v(63.07, -46.75) * mm, "end": v(63.95, -45.53) * mm});
            skLineSegment(sketch, "E46.2.40.0", {"start": v(78, -45.9) * mm, "end": v(78.75, -44.6) * mm});
            skLineSegment(sketch, "E46.3.40.0", {"start": v(68.36, -38.6) * mm, "end": v(78.75, -44.6) * mm});
            skLineSegment(sketch, "E46.6.40.0", {"start": v(67.6, -39.9) * mm, "end": v(78, -45.9) * mm});
            skLineSegment(sketch, "E46.9.40.0", {"start": v(67.6, -39.9) * mm, "end": v(68.36, -38.6) * mm});
            skLineSegment(sketch, "E46.2.41.0", {"start": v(82.37, -37.5) * mm, "end": v(82.98, -36.12) * mm});
            skLineSegment(sketch, "E46.3.41.0", {"start": v(72.02, -31.24) * mm, "end": v(82.98, -36.12) * mm});
            skLineSegment(sketch, "E46.6.41.0", {"start": v(71.4, -32.61) * mm, "end": v(82.37, -37.5) * mm});
            skLineSegment(sketch, "E46.9.41.0", {"start": v(71.4, -32.61) * mm, "end": v(72.02, -31.24) * mm});
            skLineSegment(sketch, "E46.2.42.0", {"start": v(85.84, -28.68) * mm, "end": v(86.3, -27.25) * mm});
            skLineSegment(sketch, "E46.3.42.0", {"start": v(74.89, -23.54) * mm, "end": v(86.3, -27.25) * mm});
            skLineSegment(sketch, "E46.6.42.0", {"start": v(74.43, -24.97) * mm, "end": v(85.84, -28.68) * mm});
            skLineSegment(sketch, "E46.9.42.0", {"start": v(74.43, -24.97) * mm, "end": v(74.89, -23.54) * mm});
            skLineSegment(sketch, "E46.2.43.0", {"start": v(88.37, -19.55) * mm, "end": v(88.68, -18.08) * mm});
            skLineSegment(sketch, "E46.3.43.0", {"start": v(76.94, -15.59) * mm, "end": v(88.68, -18.08) * mm});
            skLineSegment(sketch, "E46.6.43.0", {"start": v(76.63, -17.05) * mm, "end": v(88.37, -19.55) * mm});
            skLineSegment(sketch, "E46.9.43.0", {"start": v(76.63, -17.05) * mm, "end": v(76.94, -15.59) * mm});
            skLineSegment(sketch, "E46.2.44.0", {"start": v(89.93, -10.2) * mm, "end": v(90.08, -8.71) * mm});
            skLineSegment(sketch, "E46.3.44.0", {"start": v(78.15, -7.46) * mm, "end": v(90.08, -8.71) * mm});
            skLineSegment(sketch, "E46.6.44.0", {"start": v(78, -8.95) * mm, "end": v(89.93, -10.2) * mm});
            skLineSegment(sketch, "E46.9.44.0", {"start": v(78, -8.95) * mm, "end": v(78.15, -7.46) * mm});
            skLineSegment(sketch, "E46.2.45.0", {"start": v(90.5, -0.75) * mm, "end": v(90.5, 0.75) * mm});
            skLineSegment(sketch, "E46.3.45.0", {"start": v(78.5, 0.75) * mm, "end": v(90.5, 0.75) * mm});
            skLineSegment(sketch, "E46.6.45.0", {"start": v(78.5, -0.75) * mm, "end": v(90.5, -0.75) * mm});
            skLineSegment(sketch, "E46.9.45.0", {"start": v(78.5, -0.75) * mm, "end": v(78.5, 0.75) * mm});
            skLineSegment(sketch, "E46.2.46.0", {"start": v(90.08, 8.71) * mm, "end": v(89.93, 10.2) * mm});
            skLineSegment(sketch, "E46.3.46.0", {"start": v(78, 8.95) * mm, "end": v(89.93, 10.2) * mm});
            skLineSegment(sketch, "E46.6.46.0", {"start": v(78.15, 7.46) * mm, "end": v(90.08, 8.71) * mm});
            skLineSegment(sketch, "E46.9.46.0", {"start": v(78.15, 7.46) * mm, "end": v(78, 8.95) * mm});
            skLineSegment(sketch, "E46.2.47.0", {"start": v(88.68, 18.08) * mm, "end": v(88.37, 19.55) * mm});
            skLineSegment(sketch, "E46.3.47.0", {"start": v(76.63, 17.05) * mm, "end": v(88.37, 19.55) * mm});
            skLineSegment(sketch, "E46.6.47.0", {"start": v(76.94, 15.59) * mm, "end": v(88.68, 18.08) * mm});
            skLineSegment(sketch, "E46.9.47.0", {"start": v(76.94, 15.59) * mm, "end": v(76.63, 17.05) * mm});
            skLineSegment(sketch, "E46.2.48.0", {"start": v(86.3, 27.25) * mm, "end": v(85.84, 28.68) * mm});
            skLineSegment(sketch, "E46.3.48.0", {"start": v(74.43, 24.97) * mm, "end": v(85.84, 28.68) * mm});
            skLineSegment(sketch, "E46.6.48.0", {"start": v(74.89, 23.54) * mm, "end": v(86.3, 27.25) * mm});
            skLineSegment(sketch, "E46.9.48.0", {"start": v(74.89, 23.54) * mm, "end": v(74.43, 24.97) * mm});
            skLineSegment(sketch, "E46.2.49.0", {"start": v(82.98, 36.12) * mm, "end": v(82.37, 37.5) * mm});
            skLineSegment(sketch, "E46.3.49.0", {"start": v(71.4, 32.61) * mm, "end": v(82.37, 37.5) * mm});
            skLineSegment(sketch, "E46.6.49.0", {"start": v(72.02, 31.24) * mm, "end": v(82.98, 36.12) * mm});
            skLineSegment(sketch, "E46.9.49.0", {"start": v(72.02, 31.24) * mm, "end": v(71.4, 32.61) * mm});
            skLineSegment(sketch, "E46.2.50.0", {"start": v(78.75, 44.6) * mm, "end": v(78, 45.9) * mm});
            skLineSegment(sketch, "E46.3.50.0", {"start": v(67.6, 39.9) * mm, "end": v(78, 45.9) * mm});
            skLineSegment(sketch, "E46.6.50.0", {"start": v(68.36, 38.6) * mm, "end": v(78.75, 44.6) * mm});
            skLineSegment(sketch, "E46.9.50.0", {"start": v(68.36, 38.6) * mm, "end": v(67.6, 39.9) * mm});
            skLineSegment(sketch, "E46.2.51.0", {"start": v(73.66, 52.59) * mm, "end": v(72.78, 53.8) * mm});
            skLineSegment(sketch, "E46.3.51.0", {"start": v(63.07, 46.75) * mm, "end": v(72.78, 53.8) * mm});
            skLineSegment(sketch, "E46.6.51.0", {"start": v(63.95, 45.53) * mm, "end": v(73.66, 52.59) * mm});
            skLineSegment(sketch, "E46.9.51.0", {"start": v(63.95, 45.53) * mm, "end": v(63.07, 46.75) * mm});
            skLineSegment(sketch, "E46.2.52.0", {"start": v(67.76, 60) * mm, "end": v(66.75, 61.11) * mm});
            skLineSegment(sketch, "E46.3.52.0", {"start": v(57.84, 53.08) * mm, "end": v(66.75, 61.11) * mm});
            skLineSegment(sketch, "E46.6.52.0", {"start": v(58.84, 51.97) * mm, "end": v(67.76, 60) * mm});
            skLineSegment(sketch, "E46.9.52.0", {"start": v(58.84, 51.97) * mm, "end": v(57.84, 53.08) * mm});
            skLineSegment(sketch, "E46.2.53.0", {"start": v(61.11, 66.75) * mm, "end": v(60, 67.76) * mm});
            skLineSegment(sketch, "E46.3.53.0", {"start": v(51.97, 58.84) * mm, "end": v(60, 67.76) * mm});
            skLineSegment(sketch, "E46.6.53.0", {"start": v(53.08, 57.84) * mm, "end": v(61.11, 66.75) * mm});
            skLineSegment(sketch, "E46.9.53.0", {"start": v(53.08, 57.84) * mm, "end": v(51.97, 58.84) * mm});
            skLineSegment(sketch, "E46.2.54.0", {"start": v(53.8, 72.78) * mm, "end": v(52.59, 73.66) * mm});
            skLineSegment(sketch, "E46.3.54.0", {"start": v(45.53, 63.95) * mm, "end": v(52.59, 73.66) * mm});
            skLineSegment(sketch, "E46.6.54.0", {"start": v(46.75, 63.07) * mm, "end": v(53.8, 72.78) * mm});
            skLineSegment(sketch, "E46.9.54.0", {"start": v(46.75, 63.07) * mm, "end": v(45.53, 63.95) * mm});
            skLineSegment(sketch, "E46.2.55.0", {"start": v(45.9, 78) * mm, "end": v(44.6, 78.75) * mm});
            skLineSegment(sketch, "E46.3.55.0", {"start": v(38.6, 68.36) * mm, "end": v(44.6, 78.75) * mm});
            skLineSegment(sketch, "E46.6.55.0", {"start": v(39.9, 67.6) * mm, "end": v(45.9, 78) * mm});
            skLineSegment(sketch, "E46.9.55.0", {"start": v(39.9, 67.6) * mm, "end": v(38.6, 68.36) * mm});
            skLineSegment(sketch, "E46.2.56.0", {"start": v(37.5, 82.37) * mm, "end": v(36.12, 82.98) * mm});
            skLineSegment(sketch, "E46.3.56.0", {"start": v(31.24, 72.02) * mm, "end": v(36.12, 82.98) * mm});
            skLineSegment(sketch, "E46.6.56.0", {"start": v(32.61, 71.4) * mm, "end": v(37.5, 82.37) * mm});
            skLineSegment(sketch, "E46.9.56.0", {"start": v(32.61, 71.4) * mm, "end": v(31.24, 72.02) * mm});
            skLineSegment(sketch, "E46.2.57.0", {"start": v(28.68, 85.84) * mm, "end": v(27.25, 86.3) * mm});
            skLineSegment(sketch, "E46.3.57.0", {"start": v(23.54, 74.89) * mm, "end": v(27.25, 86.3) * mm});
            skLineSegment(sketch, "E46.6.57.0", {"start": v(24.97, 74.43) * mm, "end": v(28.68, 85.84) * mm});
            skLineSegment(sketch, "E46.9.57.0", {"start": v(24.97, 74.43) * mm, "end": v(23.54, 74.89) * mm});
            skLineSegment(sketch, "E46.2.58.0", {"start": v(19.55, 88.37) * mm, "end": v(18.08, 88.68) * mm});
            skLineSegment(sketch, "E46.3.58.0", {"start": v(15.59, 76.94) * mm, "end": v(18.08, 88.68) * mm});
            skLineSegment(sketch, "E46.6.58.0", {"start": v(17.05, 76.63) * mm, "end": v(19.55, 88.37) * mm});
            skLineSegment(sketch, "E46.9.58.0", {"start": v(17.05, 76.63) * mm, "end": v(15.59, 76.94) * mm});
            skLineSegment(sketch, "E46.2.59.0", {"start": v(10.2, 89.93) * mm, "end": v(8.71, 90.08) * mm});
            skLineSegment(sketch, "E46.3.59.0", {"start": v(7.46, 78.15) * mm, "end": v(8.71, 90.08) * mm});
            skLineSegment(sketch, "E46.6.59.0", {"start": v(8.95, 78) * mm, "end": v(10.2, 89.93) * mm});
            skLineSegment(sketch, "E46.9.59.0", {"start": v(8.95, 78) * mm, "end": v(7.46, 78.15) * mm});
            skSolve(sketch);
        }
        {
            var Q0;
            Q0 = qSketchRegion(id + "F27", true);
            extrude(context, id + "F28", {"entities" : qUnion([Q0]), "operationType" : NewBodyOperationType.REMOVE, "oppositeDirection" : true, "depth" : 0.2 * mm, "offsetDistance" : 25 * mm});
        }
        {
            var Q0;
            Q0=makeQuery(id+"F26.boolean.opBoolean","COPY",FACE,{"derivedFrom":makeQuery(id+"F26.opExtrude","CAP_FACE",FACE,{"disambiguationData":[OSD([sQuery(id+"F25.wireOp",EDGE,"E41.bottom"),sQuery(id+"F25.wireOp",EDGE,"E41.top"),sQuery(id+"F25.wireOp",EDGE,"E41.left"),sQuery(id+"F25.wireOp",EDGE,"E41.right")])],"isStart":false})});
            extrude(context, id + "F29", {"entities" : qUnion([Q0]), "depth" : 1 * mm, "offsetDistance" : 25 * mm});
        }
        {
            var Q0;
            Q0=makeQuery(id+"F28.boolean.opBoolean","COPY",FACE,{"derivedFrom":makeQuery(id+"F28.opExtrude","CAP_FACE",FACE,{"disambiguationData":[OSD([sQuery(id+"F27.wireOp",EDGE,"E46.2.59.0"),sQuery(id+"F27.wireOp",EDGE,"E46.3.59.0"),sQuery(id+"F27.wireOp",EDGE,"E46.6.59.0"),sQuery(id+"F27.wireOp",EDGE,"E46.9.59.0")])],"isStart":false})});
            extrude(context, id + "F30", {"entities" : qUnion([Q0]), "depth" : .4 * mm, "offsetDistance" : 25 * mm});
        }
        {
            var Q0;
            Q0=makeQuery(id+"F15.opExtrude","CAP_FACE",FACE,{"disambiguationData":[OSD([sQuery(id+"F14.wireOp",EDGE,"E21.0"),sQuery(id+"F14.wireOp",EDGE,"E22"),sQuery(id+"F14.wireOp",EDGE,"E23"),sQuery(id+"F14.wireOp",EDGE,"E24"),sQuery(id+"F14.wireOp",EDGE,"E25.MirrorCS"),sQuery(id+"F14.wireOp",EDGE,"E26.MirrorCS"),sQuery(id+"F14.wireOp",EDGE,"E27.1.0"),sQuery(id+"F14.wireOp",EDGE,"E27.1.1"),sQuery(id+"F14.wireOp",EDGE,"E27.1.2"),sQuery(id+"F14.wireOp",EDGE,"E27.1.3"),sQuery(id+"F14.wireOp",EDGE,"E27.2.0"),sQuery(id+"F14.wireOp",EDGE,"E27.2.1"),sQuery(id+"F14.wireOp",EDGE,"E27.2.2"),sQuery(id+"F14.wireOp",EDGE,"E27.2.3"),sQuery(id+"F14.wireOp",EDGE,"E28.1.3.0"),sQuery(id+"F14.wireOp",EDGE,"E28.3.3.0"),sQuery(id+"F14.wireOp",EDGE,"E28.6.3.0"),sQuery(id+"F14.wireOp",EDGE,"E28.9.3.0"),sQuery(id+"F14.wireOp",EDGE,"E28.1.4.0"),sQuery(id+"F14.wireOp",EDGE,"E28.3.4.0"),sQuery(id+"F14.wireOp",EDGE,"E28.6.4.0"),sQuery(id+"F14.wireOp",EDGE,"E28.9.4.0"),sQuery(id+"F14.wireOp",EDGE,"E28.1.5.0"),sQuery(id+"F14.wireOp",EDGE,"E28.3.5.0"),sQuery(id+"F14.wireOp",EDGE,"E28.6.5.0"),sQuery(id+"F14.wireOp",EDGE,"E28.9.5.0"),sQuery(id+"F14.wireOp",EDGE,"E28.1.6.0"),sQuery(id+"F14.wireOp",EDGE,"E28.3.6.0"),sQuery(id+"F14.wireOp",EDGE,"E28.6.6.0"),sQuery(id+"F14.wireOp",EDGE,"E28.9.6.0"),sQuery(id+"F14.wireOp",EDGE,"E28.1.7.0"),sQuery(id+"F14.wireOp",EDGE,"E28.3.7.0"),sQuery(id+"F14.wireOp",EDGE,"E28.6.7.0"),sQuery(id+"F14.wireOp",EDGE,"E28.9.7.0"),sQuery(id+"F14.wireOp",EDGE,"E28.1.8.0"),sQuery(id+"F14.wireOp",EDGE,"E28.3.8.0"),sQuery(id+"F14.wireOp",EDGE,"E28.6.8.0"),sQuery(id+"F14.wireOp",EDGE,"E28.9.8.0"),sQuery(id+"F14.wireOp",EDGE,"E28.1.9.0"),sQuery(id+"F14.wireOp",EDGE,"E28.3.9.0"),sQuery(id+"F14.wireOp",EDGE,"E28.6.9.0"),sQuery(id+"F14.wireOp",EDGE,"E28.9.9.0"),sQuery(id+"F14.wireOp",EDGE,"E28.1.10.0"),sQuery(id+"F14.wireOp",EDGE,"E28.3.10.0"),sQuery(id+"F14.wireOp",EDGE,"E28.6.10.0"),sQuery(id+"F14.wireOp",EDGE,"E28.9.10.0"),sQuery(id+"F14.wireOp",EDGE,"E28.1.11.0"),sQuery(id+"F14.wireOp",EDGE,"E28.3.11.0"),sQuery(id+"F14.wireOp",EDGE,"E28.6.11.0"),sQuery(id+"F14.wireOp",EDGE,"E28.9.11.0"),sQuery(id+"F14.wireOp",EDGE,"E28.1.12.0"),sQuery(id+"F14.wireOp",EDGE,"E28.3.12.0"),sQuery(id+"F14.wireOp",EDGE,"E28.6.12.0"),sQuery(id+"F14.wireOp",EDGE,"E28.9.12.0"),sQuery(id+"F14.wireOp",EDGE,"E28.1.13.0"),sQuery(id+"F14.wireOp",EDGE,"E28.3.13.0"),sQuery(id+"F14.wireOp",EDGE,"E28.6.13.0"),sQuery(id+"F14.wireOp",EDGE,"E28.9.13.0"),sQuery(id+"F14.wireOp",EDGE,"E28.1.14.0"),sQuery(id+"F14.wireOp",EDGE,"E28.3.14.0"),sQuery(id+"F14.wireOp",EDGE,"E28.6.14.0"),sQuery(id+"F14.wireOp",EDGE,"E28.9.14.0"),sQuery(id+"F14.wireOp",EDGE,"E28.1.15.0"),sQuery(id+"F14.wireOp",EDGE,"E28.3.15.0"),sQuery(id+"F14.wireOp",EDGE,"E28.6.15.0"),sQuery(id+"F14.wireOp",EDGE,"E28.9.15.0"),sQuery(id+"F14.wireOp",EDGE,"E28.1.16.0"),sQuery(id+"F14.wireOp",EDGE,"E28.3.16.0"),sQuery(id+"F14.wireOp",EDGE,"E28.6.16.0"),sQuery(id+"F14.wireOp",EDGE,"E28.9.16.0"),sQuery(id+"F14.wireOp",EDGE,"E28.1.17.0"),sQuery(id+"F14.wireOp",EDGE,"E28.3.17.0"),sQuery(id+"F14.wireOp",EDGE,"E28.6.17.0"),sQuery(id+"F14.wireOp",EDGE,"E28.9.17.0"),sQuery(id+"F14.wireOp",EDGE,"E28.1.18.0"),sQuery(id+"F14.wireOp",EDGE,"E28.3.18.0"),sQuery(id+"F14.wireOp",EDGE,"E28.6.18.0"),sQuery(id+"F14.wireOp",EDGE,"E28.9.18.0"),sQuery(id+"F14.wireOp",EDGE,"E28.1.19.0"),sQuery(id+"F14.wireOp",EDGE,"E28.3.19.0"),sQuery(id+"F14.wireOp",EDGE,"E28.6.19.0"),sQuery(id+"F14.wireOp",EDGE,"E28.9.19.0"),sQuery(id+"F14.wireOp",EDGE,"E28.1.20.0"),sQuery(id+"F14.wireOp",EDGE,"E28.3.20.0"),sQuery(id+"F14.wireOp",EDGE,"E28.6.20.0"),sQuery(id+"F14.wireOp",EDGE,"E28.9.20.0"),sQuery(id+"F14.wireOp",EDGE,"E28.1.21.0"),sQuery(id+"F14.wireOp",EDGE,"E28.3.21.0"),sQuery(id+"F14.wireOp",EDGE,"E28.6.21.0"),sQuery(id+"F14.wireOp",EDGE,"E28.9.21.0"),sQuery(id+"F14.wireOp",EDGE,"E28.1.22.0"),sQuery(id+"F14.wireOp",EDGE,"E28.3.22.0"),sQuery(id+"F14.wireOp",EDGE,"E28.6.22.0"),sQuery(id+"F14.wireOp",EDGE,"E28.9.22.0"),sQuery(id+"F14.wireOp",EDGE,"E28.1.23.0"),sQuery(id+"F14.wireOp",EDGE,"E28.3.23.0"),sQuery(id+"F14.wireOp",EDGE,"E28.6.23.0"),sQuery(id+"F14.wireOp",EDGE,"E28.9.23.0"),sQuery(id+"F14.wireOp",EDGE,"E28.1.24.0"),sQuery(id+"F14.wireOp",EDGE,"E28.3.24.0"),sQuery(id+"F14.wireOp",EDGE,"E28.6.24.0"),sQuery(id+"F14.wireOp",EDGE,"E28.9.24.0"),sQuery(id+"F14.wireOp",EDGE,"E28.1.25.0"),sQuery(id+"F14.wireOp",EDGE,"E28.3.25.0"),sQuery(id+"F14.wireOp",EDGE,"E28.6.25.0"),sQuery(id+"F14.wireOp",EDGE,"E28.9.25.0"),sQuery(id+"F14.wireOp",EDGE,"E28.1.26.0"),sQuery(id+"F14.wireOp",EDGE,"E28.3.26.0"),sQuery(id+"F14.wireOp",EDGE,"E28.6.26.0"),sQuery(id+"F14.wireOp",EDGE,"E28.9.26.0"),sQuery(id+"F14.wireOp",EDGE,"E28.1.27.0"),sQuery(id+"F14.wireOp",EDGE,"E28.3.27.0"),sQuery(id+"F14.wireOp",EDGE,"E28.6.27.0"),sQuery(id+"F14.wireOp",EDGE,"E28.9.27.0"),sQuery(id+"F14.wireOp",EDGE,"E28.1.28.0"),sQuery(id+"F14.wireOp",EDGE,"E28.3.28.0"),sQuery(id+"F14.wireOp",EDGE,"E28.6.28.0"),sQuery(id+"F14.wireOp",EDGE,"E28.9.28.0"),sQuery(id+"F14.wireOp",EDGE,"E28.1.29.0"),sQuery(id+"F14.wireOp",EDGE,"E28.3.29.0"),sQuery(id+"F14.wireOp",EDGE,"E28.6.29.0"),sQuery(id+"F14.wireOp",EDGE,"E28.9.29.0"),sQuery(id+"F14.wireOp",EDGE,"E28.1.30.0"),sQuery(id+"F14.wireOp",EDGE,"E28.3.30.0"),sQuery(id+"F14.wireOp",EDGE,"E28.6.30.0"),sQuery(id+"F14.wireOp",EDGE,"E28.9.30.0"),sQuery(id+"F14.wireOp",EDGE,"E28.1.31.0"),sQuery(id+"F14.wireOp",EDGE,"E28.3.31.0"),sQuery(id+"F14.wireOp",EDGE,"E28.6.31.0"),sQuery(id+"F14.wireOp",EDGE,"E28.9.31.0"),sQuery(id+"F14.wireOp",EDGE,"E28.1.32.0"),sQuery(id+"F14.wireOp",EDGE,"E28.3.32.0"),sQuery(id+"F14.wireOp",EDGE,"E28.6.32.0"),sQuery(id+"F14.wireOp",EDGE,"E28.9.32.0"),sQuery(id+"F14.wireOp",EDGE,"E28.1.33.0"),sQuery(id+"F14.wireOp",EDGE,"E28.3.33.0"),sQuery(id+"F14.wireOp",EDGE,"E28.6.33.0"),sQuery(id+"F14.wireOp",EDGE,"E28.9.33.0"),sQuery(id+"F14.wireOp",EDGE,"E28.1.34.0"),sQuery(id+"F14.wireOp",EDGE,"E28.3.34.0"),sQuery(id+"F14.wireOp",EDGE,"E28.6.34.0"),sQuery(id+"F14.wireOp",EDGE,"E28.9.34.0"),sQuery(id+"F14.wireOp",EDGE,"E28.1.35.0"),sQuery(id+"F14.wireOp",EDGE,"E28.3.35.0"),sQuery(id+"F14.wireOp",EDGE,"E28.6.35.0"),sQuery(id+"F14.wireOp",EDGE,"E28.9.35.0"),sQuery(id+"F14.wireOp",EDGE,"E28.1.36.0"),sQuery(id+"F14.wireOp",EDGE,"E28.3.36.0"),sQuery(id+"F14.wireOp",EDGE,"E28.6.36.0"),sQuery(id+"F14.wireOp",EDGE,"E28.9.36.0"),sQuery(id+"F14.wireOp",EDGE,"E28.1.37.0"),sQuery(id+"F14.wireOp",EDGE,"E28.3.37.0"),sQuery(id+"F14.wireOp",EDGE,"E28.6.37.0"),sQuery(id+"F14.wireOp",EDGE,"E28.9.37.0"),sQuery(id+"F14.wireOp",EDGE,"E28.1.38.0"),sQuery(id+"F14.wireOp",EDGE,"E28.3.38.0"),sQuery(id+"F14.wireOp",EDGE,"E28.6.38.0"),sQuery(id+"F14.wireOp",EDGE,"E28.9.38.0"),sQuery(id+"F14.wireOp",EDGE,"E28.1.39.0"),sQuery(id+"F14.wireOp",EDGE,"E28.3.39.0"),sQuery(id+"F14.wireOp",EDGE,"E28.6.39.0"),sQuery(id+"F14.wireOp",EDGE,"E28.9.39.0")])],"isStart":false});
            var sketch = newSketch(context, id + "F31", { "sketchPlane" : qUnion([Q0])});
            skCircle(sketch, "E47.0.0", {"center": v(0, 0) * mm, "radius": 3 * mm});
            skCircle(sketch, "E48.0", {"center": v(0, 0) * mm, "radius": 5 * mm});
            skSolve(sketch);
        }
        {
            var Q0;
            Q0 = qSketchRegion(id + "F31", true);
            extrude(context, id + "F32", {"entities" : qUnion([Q0]), "operationType" : NewBodyOperationType.ADD, "depth" : 5 * mm, "offsetDistance" : 25 * mm});
        }
        {
            var Q0;
            Q0=makeQuery(id+"F32.opExtrude","CAP_FACE",FACE,{"disambiguationData":[OSD([sQuery(id+"F31.wireOp",EDGE,"E47.0.0"),sQuery(id+"F31.wireOp",EDGE,"E48.0")])],"isStart":false});
            var sketch = newSketch(context, id + "F33", { "sketchPlane" : qUnion([Q0])});
            skCircle(sketch, "E49.0", {"center": v(0, 0) * mm, "radius": 3 * mm});
            skCircle(sketch, "E50.0", {"center": v(0, 0) * mm, "radius": 5 * mm});
            skLineSegment(sketch, "E51", {"start": v(3, 4) * mm, "end": v(1.5, 50) * mm});
            skLineSegment(sketch, "E52", {"start": v(1.5, 50) * mm, "end": v(0, 50) * mm});
            skLineSegment(sketch, "E53.MirrorCS", {"start": v(-1.5, 50) * mm, "end": v(0, 50) * mm});
            skLineSegment(sketch, "E54.MirrorCS", {"start": v(-3, 4) * mm, "end": v(-1.5, 50) * mm});
            skSolve(sketch);
        }
        {
            var Q0;
            Q0 = qSketchRegion(id + "F33", true);
            extrude(context, id + "F34", {"entities" : qUnion([Q0]), "operationType" : NewBodyOperationType.ADD, "depth" : 1 * mm, "offsetDistance" : 25 * mm});
        }
        {
            var Q0;
            Q0=makeQuery(id+"F6.opExtrude","CAP_FACE",FACE,{"disambiguationData":[OSD([sQuery(id+"F0.wireOp",EDGE,"E0")])],"isStart":false});
            var sketch = newSketch(context, id + "F35", { "sketchPlane" : qUnion([Q0])});
            skCircle(sketch, "E55", {"center": v(0, 0) * mm, "radius": 5 * mm});
            skLineSegment(sketch, "E56", {"start": v(2, 4.58) * mm, "end": v(0.5, 80) * mm});
            skLineSegment(sketch, "E57", {"start": v(0.5, 80) * mm, "end": v(0, 80) * mm});
            skLineSegment(sketch, "E58.MirrorCS", {"start": v(-0.5, 80) * mm, "end": v(0, 80) * mm});
            skLineSegment(sketch, "E59.MirrorCS", {"start": v(-2, 4.58) * mm, "end": v(-0.5, 80) * mm});
            skSolve(sketch);
        }
        {
            var Q0;
            Q0 = qSketchRegion(id + "F35", true);
            extrude(context, id + "F36", {"entities" : qUnion([Q0]), "operationType" : NewBodyOperationType.ADD, "oppositeDirection" : true, "depth" : 1 * mm, "offsetDistance" : 25 * mm});
        }
    });
